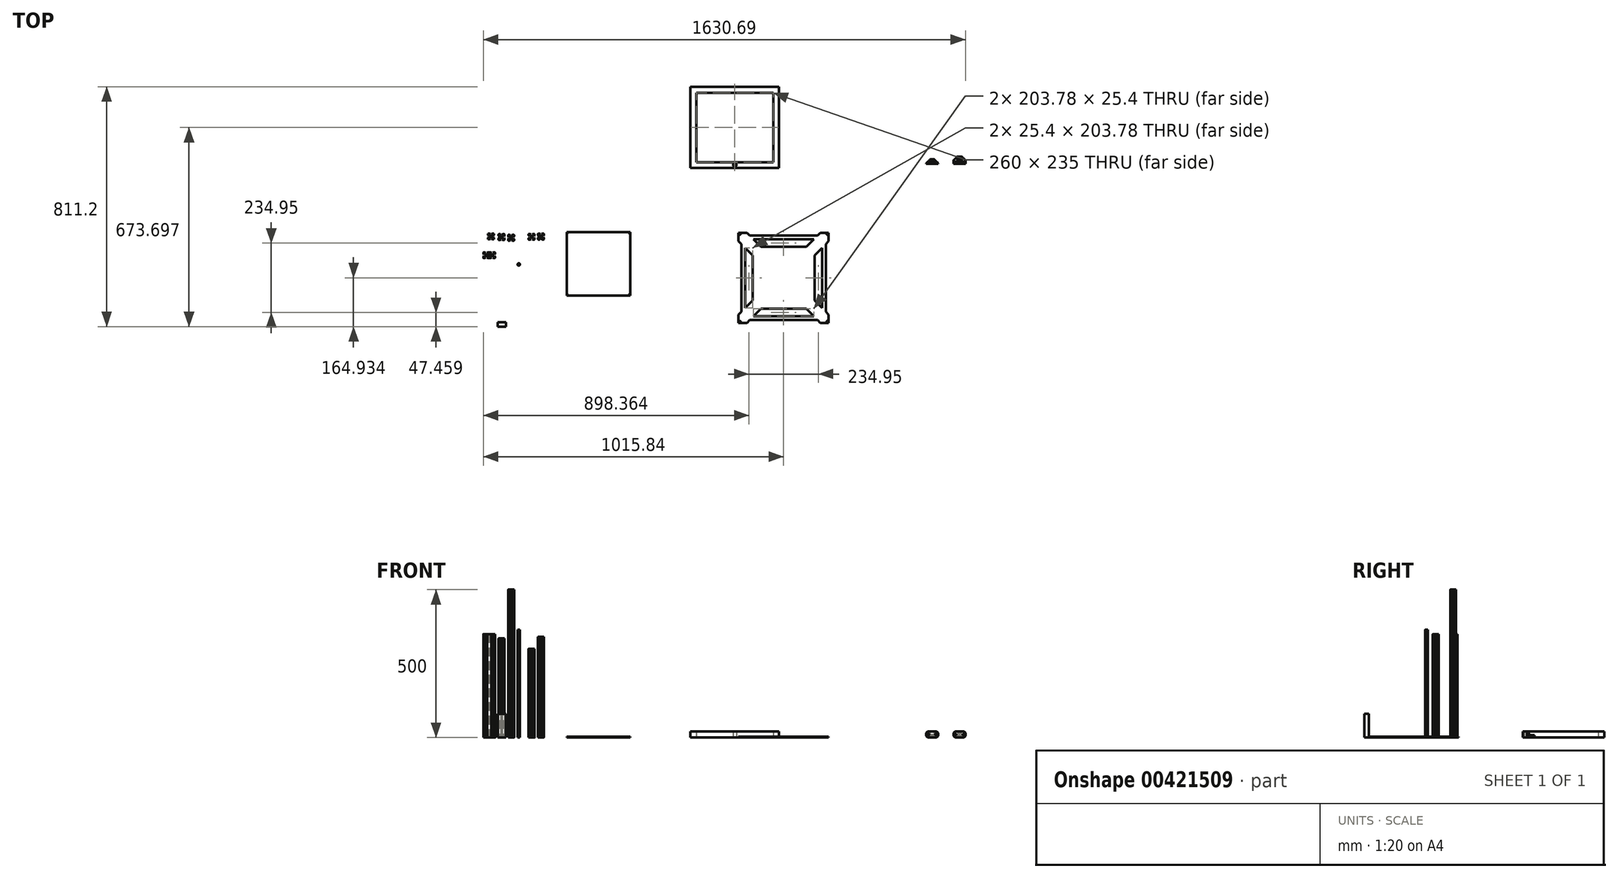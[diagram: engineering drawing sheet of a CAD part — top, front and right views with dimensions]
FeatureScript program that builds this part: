
annotation { "Feature Type Name" : "Feature", "Feature Type Description" : "" }
export const myFeature = defineFeature(function(context is Context, id is Id, definition is map)
    precondition{}
    {
        {
            var Q0;
            Q0=qCreatedBy(makeId("Top.planeOp"),FACE);
            var sketch = newSketch(context, id + "F0", { "sketchPlane" : qUnion([Q0])});
            skArc(sketch, "E0.0", {"start": v(-58.83, 50.5) * mm, "mid": v(-59.9, 50.06) * mm, "end": v(-60.33, 49) * mm});
            skLineSegment(sketch, "E1.0", {"start": v(-60.33, 49) * mm, "end": v(-60.33, 45.4) * mm});
            skLineSegment(sketch, "E2.0", {"start": v(-56.9, 48.7) * mm, "end": v(-58.53, 48.7) * mm});
            skLineSegment(sketch, "E3.0", {"start": v(-56.9, 48.16) * mm, "end": v(-56.9, 48.7) * mm});
            skLineSegment(sketch, "E4.0", {"start": v(-58, 47.07) * mm, "end": v(-56.9, 48.16) * mm});
            skLineSegment(sketch, "E5.0", {"start": v(-58.53, 47.07) * mm, "end": v(-58, 47.07) * mm});
            skLineSegment(sketch, "E6.0", {"start": v(-58.53, 48.7) * mm, "end": v(-58.53, 47.07) * mm});
            skArc(sketch, "E7.0", {"start": v(-54.68, 50.26) * mm, "mid": v(-54.93, 50.44) * mm, "end": v(-55.24, 50.5) * mm});
            skLineSegment(sketch, "E8.0", {"start": v(-55.24, 50.5) * mm, "end": v(-58.83, 50.5) * mm});
            skLineSegment(sketch, "E9.0", {"start": v(-55.83, 47.06) * mm, "end": v(-55.83, 48.7) * mm});
            skLineSegment(sketch, "E10.0", {"start": v(-55.83, 48.7) * mm, "end": v(-53.22, 48.7) * mm});
            skLineSegment(sketch, "E11.0", {"start": v(-53.22, 48.8) * mm, "end": v(-54.68, 50.26) * mm});
            skLineSegment(sketch, "E12.0", {"start": v(-53.22, 48.7) * mm, "end": v(-53.22, 48.8) * mm});
            skLineSegment(sketch, "E13.0", {"start": v(-52.67, 43.9) * mm, "end": v(-55.83, 47.06) * mm});
            skLineSegment(sketch, "E14.0", {"start": v(-56.9, 46) * mm, "end": v(-53.73, 42.84) * mm});
            skLineSegment(sketch, "E15.0", {"start": v(-58.53, 46) * mm, "end": v(-56.9, 46) * mm});
            skArc(sketch, "E16.0", {"start": v(-60.33, 45.4) * mm, "mid": v(-60.27, 45.1) * mm, "end": v(-60.1, 44.84) * mm});
            skLineSegment(sketch, "E17.0", {"start": v(-60.1, 44.84) * mm, "end": v(-58.64, 43.39) * mm});
            skLineSegment(sketch, "E18.0", {"start": v(-58.64, 43.39) * mm, "end": v(-58.53, 43.39) * mm});
            skLineSegment(sketch, "E19.0", {"start": v(-58.53, 43.39) * mm, "end": v(-58.53, 46) * mm});
            skLineSegment(sketch, "E20.0", {"start": v(-53.73, 42.84) * mm, "end": v(-53.73, 38.16) * mm});
            skLineSegment(sketch, "E21.0", {"start": v(-48, 43.9) * mm, "end": v(-52.67, 43.9) * mm});
            skCircle(sketch, "E22.0", {"center": v(-50.33, 40.5) * mm, "radius": 2.1 * mm});
            skLineSegment(sketch, "E23.0", {"start": v(-45.98, 50.26) * mm, "end": v(-47.44, 48.8) * mm});
            skLineSegment(sketch, "E24.0", {"start": v(-47.44, 48.7) * mm, "end": v(-44.83, 48.7) * mm});
            skLineSegment(sketch, "E25.0", {"start": v(-44.83, 48.7) * mm, "end": v(-44.83, 47.06) * mm});
            skLineSegment(sketch, "E26.0", {"start": v(-44.83, 47.06) * mm, "end": v(-48, 43.9) * mm});
            skLineSegment(sketch, "E27.0", {"start": v(-46.93, 42.84) * mm, "end": v(-43.77, 46) * mm});
            skLineSegment(sketch, "E28.0", {"start": v(-43.77, 46) * mm, "end": v(-42.13, 46) * mm});
            skLineSegment(sketch, "E29.0", {"start": v(-42.13, 46) * mm, "end": v(-42.13, 43.39) * mm});
            skLineSegment(sketch, "E30.0", {"start": v(-42.13, 47.07) * mm, "end": v(-42.13, 48.7) * mm});
            skLineSegment(sketch, "E31.0", {"start": v(-42.67, 47.07) * mm, "end": v(-42.13, 47.07) * mm});
            skLineSegment(sketch, "E32.0", {"start": v(-43.76, 48.16) * mm, "end": v(-42.67, 47.07) * mm});
            skLineSegment(sketch, "E33.0", {"start": v(-43.76, 48.7) * mm, "end": v(-43.76, 48.16) * mm});
            skLineSegment(sketch, "E34.0", {"start": v(-42.13, 48.7) * mm, "end": v(-43.76, 48.7) * mm});
            skArc(sketch, "E35.0", {"start": v(-45.42, 50.5) * mm, "mid": v(-45.73, 50.44) * mm, "end": v(-45.98, 50.26) * mm});
            skLineSegment(sketch, "E36.0", {"start": v(-41.83, 50.5) * mm, "end": v(-45.42, 50.5) * mm});
            skArc(sketch, "E37.0", {"start": v(-40.33, 49) * mm, "mid": v(-40.77, 50.06) * mm, "end": v(-41.83, 50.5) * mm});
            skLineSegment(sketch, "E38.0", {"start": v(-40.33, 45.4) * mm, "end": v(-40.33, 49) * mm});
            skArc(sketch, "E39.0", {"start": v(-40.56, 44.84) * mm, "mid": v(-40.4, 45.1) * mm, "end": v(-40.33, 45.4) * mm});
            skLineSegment(sketch, "E40.0", {"start": v(-42.02, 43.39) * mm, "end": v(-40.56, 44.84) * mm});
            skLineSegment(sketch, "E41.0", {"start": v(-42.13, 43.39) * mm, "end": v(-42.02, 43.39) * mm});
            skLineSegment(sketch, "E42.0", {"start": v(-46.93, 38.16) * mm, "end": v(-46.93, 42.84) * mm});
            skLineSegment(sketch, "E43.0", {"start": v(-43.77, 35) * mm, "end": v(-46.93, 38.16) * mm});
            skLineSegment(sketch, "E44.0", {"start": v(-42.13, 35) * mm, "end": v(-43.77, 35) * mm});
            skLineSegment(sketch, "E45.0", {"start": v(-42.13, 37.6) * mm, "end": v(-42.13, 35) * mm});
            skLineSegment(sketch, "E46.0", {"start": v(-42.02, 37.6) * mm, "end": v(-42.13, 37.6) * mm});
            skLineSegment(sketch, "E47.0", {"start": v(-40.56, 36.15) * mm, "end": v(-42.02, 37.6) * mm});
            skArc(sketch, "E48.0", {"start": v(-40.33, 35.59) * mm, "mid": v(-40.4, 35.9) * mm, "end": v(-40.56, 36.15) * mm});
            skLineSegment(sketch, "E49.0", {"start": v(-40.33, 32) * mm, "end": v(-40.33, 35.59) * mm});
            skLineSegment(sketch, "E50.0", {"start": v(-42.13, 33.93) * mm, "end": v(-42.67, 33.93) * mm});
            skLineSegment(sketch, "E51.0", {"start": v(-42.67, 33.93) * mm, "end": v(-43.76, 32.84) * mm});
            skLineSegment(sketch, "E52.0", {"start": v(-43.76, 32.84) * mm, "end": v(-43.76, 32.3) * mm});
            skLineSegment(sketch, "E53.0", {"start": v(-43.76, 32.3) * mm, "end": v(-42.13, 32.3) * mm});
            skLineSegment(sketch, "E54.0", {"start": v(-42.13, 32.3) * mm, "end": v(-42.13, 33.93) * mm});
            skArc(sketch, "E55.0", {"start": v(-41.83, 30.5) * mm, "mid": v(-40.77, 30.94) * mm, "end": v(-40.33, 32) * mm});
            skLineSegment(sketch, "E56.0.2", {"start": v(-53.73, 38.16) * mm, "end": v(-56.9, 35) * mm});
            skLineSegment(sketch, "E56.0.3", {"start": v(-56.9, 35) * mm, "end": v(-58.53, 35) * mm});
            skLineSegment(sketch, "E56.0.4", {"start": v(-58.53, 35) * mm, "end": v(-58.53, 37.6) * mm});
            skLineSegment(sketch, "E56.0.5", {"start": v(-58.53, 37.6) * mm, "end": v(-58.64, 37.6) * mm});
            skLineSegment(sketch, "E56.0.6", {"start": v(-58.64, 37.6) * mm, "end": v(-60.1, 36.15) * mm});
            skArc(sketch, "E56.0.7", {"start": v(-60.1, 36.15) * mm, "mid": v(-60.27, 35.9) * mm, "end": v(-60.33, 35.59) * mm});
            skLineSegment(sketch, "E56.0.8", {"start": v(-60.33, 35.59) * mm, "end": v(-60.33, 32) * mm});
            skArc(sketch, "E56.0.9", {"start": v(-60.33, 32) * mm, "mid": v(-59.9, 30.94) * mm, "end": v(-58.83, 30.5) * mm});
            skLineSegment(sketch, "E56.0.10", {"start": v(-58.83, 30.5) * mm, "end": v(-55.24, 30.5) * mm});
            skArc(sketch, "E56.0.11", {"start": v(-55.24, 30.5) * mm, "mid": v(-54.93, 30.56) * mm, "end": v(-54.68, 30.73) * mm});
            skLineSegment(sketch, "E56.0.12", {"start": v(-54.68, 30.73) * mm, "end": v(-53.22, 32.19) * mm});
            skLineSegment(sketch, "E56.0.13", {"start": v(-53.22, 32.19) * mm, "end": v(-53.22, 32.3) * mm});
            skLineSegment(sketch, "E56.0.14", {"start": v(-53.22, 32.3) * mm, "end": v(-55.83, 32.3) * mm});
            skLineSegment(sketch, "E56.0.15", {"start": v(-55.83, 32.3) * mm, "end": v(-55.83, 33.94) * mm});
            skLineSegment(sketch, "E56.0.16", {"start": v(-55.83, 33.94) * mm, "end": v(-52.67, 37.1) * mm});
            skLineSegment(sketch, "E56.0.17", {"start": v(-52.67, 37.1) * mm, "end": v(-48, 37.1) * mm});
            skLineSegment(sketch, "E56.0.18", {"start": v(-48, 37.1) * mm, "end": v(-44.83, 33.94) * mm});
            skLineSegment(sketch, "E56.0.19", {"start": v(-44.83, 33.94) * mm, "end": v(-44.83, 32.3) * mm});
            skLineSegment(sketch, "E56.0.20", {"start": v(-44.83, 32.3) * mm, "end": v(-47.44, 32.3) * mm});
            skLineSegment(sketch, "E56.0.21", {"start": v(-47.44, 32.3) * mm, "end": v(-47.44, 32.19) * mm});
            skLineSegment(sketch, "E56.0.22", {"start": v(-47.44, 32.19) * mm, "end": v(-45.98, 30.73) * mm});
            skArc(sketch, "E56.0.23", {"start": v(-45.98, 30.73) * mm, "mid": v(-45.73, 30.56) * mm, "end": v(-45.42, 30.5) * mm});
            skLineSegment(sketch, "E56.0.24", {"start": v(-45.42, 30.5) * mm, "end": v(-41.83, 30.5) * mm});
            skLineSegment(sketch, "E56.0.45", {"start": v(-47.44, 48.8) * mm, "end": v(-47.44, 48.7) * mm});
            skLineSegment(sketch, "E57.0", {"start": v(-58, 33.93) * mm, "end": v(-58.53, 33.93) * mm});
            skLineSegment(sketch, "E58.0", {"start": v(-58.53, 33.93) * mm, "end": v(-58.53, 32.3) * mm});
            skLineSegment(sketch, "E59.0", {"start": v(-58.53, 32.3) * mm, "end": v(-56.9, 32.3) * mm});
            skLineSegment(sketch, "E60.0", {"start": v(-56.9, 32.3) * mm, "end": v(-56.9, 32.84) * mm});
            skLineSegment(sketch, "E61.0", {"start": v(-56.9, 32.84) * mm, "end": v(-58, 33.93) * mm});
            skLineSegment(sketch, "E62", {"start": v(-60.33, 49) * mm, "end": v(-60.33, 50.5) * mm});
            skLineSegment(sketch, "E63", {"start": v(-60.33, 50.5) * mm, "end": v(-58.83, 50.5) * mm});
            skLineSegment(sketch, "E64", {"start": v(-41.83, 50.5) * mm, "end": v(-40.33, 50.5) * mm});
            skLineSegment(sketch, "E65", {"start": v(-40.33, 50.5) * mm, "end": v(-40.33, 49) * mm});
            skLineSegment(sketch, "E66", {"start": v(-40.33, 32) * mm, "end": v(-40.33, 30.5) * mm});
            skLineSegment(sketch, "E67", {"start": v(-40.33, 30.5) * mm, "end": v(-41.83, 30.5) * mm});
            skLineSegment(sketch, "E68", {"start": v(-58.83, 30.5) * mm, "end": v(-60.33, 30.5) * mm});
            skLineSegment(sketch, "E69", {"start": v(-60.33, 30.5) * mm, "end": v(-60.33, 32) * mm});
            skSolve(sketch);
        }
        {
            var Q0;
            Q0=qCreatedBy(makeId("Top.planeOp"),FACE);
            var sketch = newSketch(context, id + "F1", { "sketchPlane" : qUnion([Q0])});
            skArc(sketch, "E70.0", {"start": v(-23.11, 48.38) * mm, "mid": v(-24.17, 47.94) * mm, "end": v(-24.61, 46.88) * mm});
            skLineSegment(sketch, "E71.0", {"start": v(-24.61, 46.88) * mm, "end": v(-24.61, 43.29) * mm});
            skLineSegment(sketch, "E72.0", {"start": v(-21.18, 46.58) * mm, "end": v(-22.81, 46.58) * mm});
            skLineSegment(sketch, "E73.0", {"start": v(-21.18, 46.04) * mm, "end": v(-21.18, 46.58) * mm});
            skLineSegment(sketch, "E74.0", {"start": v(-22.27, 44.95) * mm, "end": v(-21.18, 46.04) * mm});
            skLineSegment(sketch, "E75.0", {"start": v(-22.81, 44.95) * mm, "end": v(-22.27, 44.95) * mm});
            skLineSegment(sketch, "E76.0", {"start": v(-22.81, 46.58) * mm, "end": v(-22.81, 44.95) * mm});
            skArc(sketch, "E77.0", {"start": v(-18.96, 48.15) * mm, "mid": v(-19.22, 48.32) * mm, "end": v(-19.52, 48.38) * mm});
            skLineSegment(sketch, "E78.0", {"start": v(-19.52, 48.38) * mm, "end": v(-23.11, 48.38) * mm});
            skLineSegment(sketch, "E79.0", {"start": v(-20.11, 44.94) * mm, "end": v(-20.11, 46.58) * mm});
            skLineSegment(sketch, "E80.0", {"start": v(-20.11, 46.58) * mm, "end": v(-17.5, 46.58) * mm});
            skLineSegment(sketch, "E81.0", {"start": v(-17.5, 46.7) * mm, "end": v(-18.96, 48.15) * mm});
            skLineSegment(sketch, "E82.0", {"start": v(-17.5, 46.58) * mm, "end": v(-17.5, 46.7) * mm});
            skLineSegment(sketch, "E83.0", {"start": v(-16.95, 41.78) * mm, "end": v(-20.11, 44.94) * mm});
            skLineSegment(sketch, "E84.0", {"start": v(-21.17, 43.88) * mm, "end": v(-18.01, 40.72) * mm});
            skLineSegment(sketch, "E85.0", {"start": v(-22.81, 43.88) * mm, "end": v(-21.17, 43.88) * mm});
            skArc(sketch, "E86.0", {"start": v(-24.61, 43.29) * mm, "mid": v(-24.55, 42.99) * mm, "end": v(-24.38, 42.73) * mm});
            skLineSegment(sketch, "E87.0", {"start": v(-24.38, 42.73) * mm, "end": v(-22.92, 41.27) * mm});
            skLineSegment(sketch, "E88.0", {"start": v(-22.92, 41.27) * mm, "end": v(-22.81, 41.27) * mm});
            skLineSegment(sketch, "E89.0", {"start": v(-22.81, 41.27) * mm, "end": v(-22.81, 43.88) * mm});
            skLineSegment(sketch, "E90.0", {"start": v(-18.01, 40.72) * mm, "end": v(-18.01, 36.04) * mm});
            skLineSegment(sketch, "E91.0", {"start": v(-12.27, 41.78) * mm, "end": v(-16.95, 41.78) * mm});
            skCircle(sketch, "E92.0", {"center": v(-14.61, 38.38) * mm, "radius": 2.1 * mm});
            skLineSegment(sketch, "E93.0", {"start": v(-10.26, 48.15) * mm, "end": v(-11.72, 46.7) * mm});
            skLineSegment(sketch, "E94.0", {"start": v(-11.72, 46.58) * mm, "end": v(-9.11, 46.58) * mm});
            skLineSegment(sketch, "E95.0", {"start": v(-9.11, 46.58) * mm, "end": v(-9.11, 44.94) * mm});
            skLineSegment(sketch, "E96.0", {"start": v(-9.11, 44.94) * mm, "end": v(-12.27, 41.78) * mm});
            skLineSegment(sketch, "E97.0", {"start": v(-11.21, 40.72) * mm, "end": v(-8.05, 43.88) * mm});
            skLineSegment(sketch, "E98.0", {"start": v(-8.05, 43.88) * mm, "end": v(-6.41, 43.88) * mm});
            skLineSegment(sketch, "E99.0", {"start": v(-6.41, 43.88) * mm, "end": v(-6.41, 41.27) * mm});
            skLineSegment(sketch, "E100.0", {"start": v(-6.41, 44.95) * mm, "end": v(-6.41, 46.58) * mm});
            skLineSegment(sketch, "E101.0", {"start": v(-6.95, 44.95) * mm, "end": v(-6.41, 44.95) * mm});
            skLineSegment(sketch, "E102.0", {"start": v(-8.04, 46.04) * mm, "end": v(-6.95, 44.95) * mm});
            skLineSegment(sketch, "E103.0", {"start": v(-8.04, 46.58) * mm, "end": v(-8.04, 46.04) * mm});
            skLineSegment(sketch, "E104.0", {"start": v(-6.41, 46.58) * mm, "end": v(-8.04, 46.58) * mm});
            skArc(sketch, "E105.0", {"start": v(-9.7, 48.38) * mm, "mid": v(-10, 48.32) * mm, "end": v(-10.26, 48.15) * mm});
            skLineSegment(sketch, "E106.0", {"start": v(-6.11, 48.38) * mm, "end": v(-9.7, 48.38) * mm});
            skArc(sketch, "E107.0", {"start": v(-4.61, 46.88) * mm, "mid": v(-5.05, 47.94) * mm, "end": v(-6.11, 48.38) * mm});
            skLineSegment(sketch, "E108.0", {"start": v(-4.61, 43.29) * mm, "end": v(-4.61, 46.88) * mm});
            skArc(sketch, "E109.0", {"start": v(-4.84, 42.73) * mm, "mid": v(-4.67, 42.99) * mm, "end": v(-4.61, 43.29) * mm});
            skLineSegment(sketch, "E110.0", {"start": v(-6.3, 41.27) * mm, "end": v(-4.84, 42.73) * mm});
            skLineSegment(sketch, "E111.0", {"start": v(-6.41, 41.27) * mm, "end": v(-6.3, 41.27) * mm});
            skLineSegment(sketch, "E112.0", {"start": v(-11.21, 36.04) * mm, "end": v(-11.21, 40.72) * mm});
            skLineSegment(sketch, "E113.0", {"start": v(-8.05, 32.88) * mm, "end": v(-11.21, 36.04) * mm});
            skLineSegment(sketch, "E114.0", {"start": v(-6.41, 32.88) * mm, "end": v(-8.05, 32.88) * mm});
            skLineSegment(sketch, "E115.0", {"start": v(-6.41, 35.5) * mm, "end": v(-6.41, 32.88) * mm});
            skLineSegment(sketch, "E116.0", {"start": v(-6.3, 35.5) * mm, "end": v(-6.41, 35.5) * mm});
            skLineSegment(sketch, "E117.0", {"start": v(-4.84, 34.03) * mm, "end": v(-6.3, 35.5) * mm});
            skArc(sketch, "E118.0", {"start": v(-4.61, 33.47) * mm, "mid": v(-4.67, 33.78) * mm, "end": v(-4.84, 34.03) * mm});
            skLineSegment(sketch, "E119.0", {"start": v(-4.61, 29.88) * mm, "end": v(-4.61, 33.47) * mm});
            skLineSegment(sketch, "E120.0", {"start": v(-6.41, 31.81) * mm, "end": v(-6.95, 31.81) * mm});
            skLineSegment(sketch, "E121.0", {"start": v(-6.95, 31.81) * mm, "end": v(-8.04, 30.72) * mm});
            skLineSegment(sketch, "E122.0", {"start": v(-8.04, 30.72) * mm, "end": v(-8.04, 30.18) * mm});
            skLineSegment(sketch, "E123.0", {"start": v(-8.04, 30.18) * mm, "end": v(-6.41, 30.18) * mm});
            skLineSegment(sketch, "E124.0", {"start": v(-6.41, 30.18) * mm, "end": v(-6.41, 31.81) * mm});
            skArc(sketch, "E125.0", {"start": v(-6.11, 28.38) * mm, "mid": v(-5.05, 28.82) * mm, "end": v(-4.61, 29.88) * mm});
            skLineSegment(sketch, "E126.0.2", {"start": v(-18.01, 36.04) * mm, "end": v(-21.17, 32.88) * mm});
            skLineSegment(sketch, "E126.0.3", {"start": v(-21.17, 32.88) * mm, "end": v(-22.81, 32.88) * mm});
            skLineSegment(sketch, "E126.0.4", {"start": v(-22.81, 32.88) * mm, "end": v(-22.81, 35.5) * mm});
            skLineSegment(sketch, "E126.0.5", {"start": v(-22.81, 35.5) * mm, "end": v(-22.92, 35.5) * mm});
            skLineSegment(sketch, "E126.0.6", {"start": v(-22.92, 35.5) * mm, "end": v(-24.38, 34.03) * mm});
            skArc(sketch, "E126.0.7", {"start": v(-24.38, 34.03) * mm, "mid": v(-24.55, 33.78) * mm, "end": v(-24.61, 33.47) * mm});
            skLineSegment(sketch, "E126.0.8", {"start": v(-24.61, 33.47) * mm, "end": v(-24.61, 29.88) * mm});
            skArc(sketch, "E126.0.9", {"start": v(-24.61, 29.88) * mm, "mid": v(-24.17, 28.82) * mm, "end": v(-23.11, 28.38) * mm});
            skLineSegment(sketch, "E126.0.10", {"start": v(-23.11, 28.38) * mm, "end": v(-19.52, 28.38) * mm});
            skArc(sketch, "E126.0.11", {"start": v(-19.52, 28.38) * mm, "mid": v(-19.22, 28.44) * mm, "end": v(-18.96, 28.61) * mm});
            skLineSegment(sketch, "E126.0.12", {"start": v(-18.96, 28.61) * mm, "end": v(-17.5, 30.07) * mm});
            skLineSegment(sketch, "E126.0.13", {"start": v(-17.5, 30.07) * mm, "end": v(-17.5, 30.18) * mm});
            skLineSegment(sketch, "E126.0.14", {"start": v(-17.5, 30.18) * mm, "end": v(-20.11, 30.18) * mm});
            skLineSegment(sketch, "E126.0.15", {"start": v(-20.11, 30.18) * mm, "end": v(-20.11, 31.82) * mm});
            skLineSegment(sketch, "E126.0.16", {"start": v(-20.11, 31.82) * mm, "end": v(-16.95, 34.98) * mm});
            skLineSegment(sketch, "E126.0.17", {"start": v(-16.95, 34.98) * mm, "end": v(-12.27, 34.98) * mm});
            skLineSegment(sketch, "E126.0.18", {"start": v(-12.27, 34.98) * mm, "end": v(-9.11, 31.82) * mm});
            skLineSegment(sketch, "E126.0.19", {"start": v(-9.11, 31.82) * mm, "end": v(-9.11, 30.18) * mm});
            skLineSegment(sketch, "E126.0.20", {"start": v(-9.11, 30.18) * mm, "end": v(-11.72, 30.18) * mm});
            skLineSegment(sketch, "E126.0.21", {"start": v(-11.72, 30.18) * mm, "end": v(-11.72, 30.07) * mm});
            skLineSegment(sketch, "E126.0.22", {"start": v(-11.72, 30.07) * mm, "end": v(-10.26, 28.61) * mm});
            skArc(sketch, "E126.0.23", {"start": v(-10.26, 28.61) * mm, "mid": v(-10, 28.44) * mm, "end": v(-9.7, 28.38) * mm});
            skLineSegment(sketch, "E126.0.24", {"start": v(-9.7, 28.38) * mm, "end": v(-6.11, 28.38) * mm});
            skLineSegment(sketch, "E126.0.45", {"start": v(-11.72, 46.7) * mm, "end": v(-11.72, 46.58) * mm});
            skLineSegment(sketch, "E127.0", {"start": v(-22.27, 31.81) * mm, "end": v(-22.81, 31.81) * mm});
            skLineSegment(sketch, "E128.0", {"start": v(-22.81, 31.81) * mm, "end": v(-22.81, 30.18) * mm});
            skLineSegment(sketch, "E129.0", {"start": v(-22.81, 30.18) * mm, "end": v(-21.18, 30.18) * mm});
            skLineSegment(sketch, "E130.0", {"start": v(-21.18, 30.18) * mm, "end": v(-21.18, 30.72) * mm});
            skLineSegment(sketch, "E131.0", {"start": v(-21.18, 30.72) * mm, "end": v(-22.27, 31.81) * mm});
            skSolve(sketch);
        }
        {
            var Q0;
            Q0=qCreatedBy(makeId("Top.planeOp"),FACE);
            var sketch = newSketch(context, id + "F2", { "sketchPlane" : qUnion([Q0])});
            skArc(sketch, "E132.0", {"start": v(9.31, 46.03) * mm, "mid": v(8.25, 45.6) * mm, "end": v(7.81, 44.53) * mm});
            skLineSegment(sketch, "E133.0", {"start": v(7.81, 44.53) * mm, "end": v(7.81, 40.94) * mm});
            skLineSegment(sketch, "E134.0", {"start": v(11.24, 44.23) * mm, "end": v(9.61, 44.23) * mm});
            skLineSegment(sketch, "E135.0", {"start": v(11.24, 43.7) * mm, "end": v(11.24, 44.23) * mm});
            skLineSegment(sketch, "E136.0", {"start": v(10.15, 42.6) * mm, "end": v(11.24, 43.7) * mm});
            skLineSegment(sketch, "E137.0", {"start": v(9.61, 42.6) * mm, "end": v(10.15, 42.6) * mm});
            skLineSegment(sketch, "E138.0", {"start": v(9.61, 44.23) * mm, "end": v(9.61, 42.6) * mm});
            skArc(sketch, "E139.0", {"start": v(13.46, 45.8) * mm, "mid": v(13.2, 45.97) * mm, "end": v(12.9, 46.03) * mm});
            skLineSegment(sketch, "E140.0", {"start": v(12.9, 46.03) * mm, "end": v(9.31, 46.03) * mm});
            skLineSegment(sketch, "E141.0", {"start": v(12.31, 42.6) * mm, "end": v(12.31, 44.23) * mm});
            skLineSegment(sketch, "E142.0", {"start": v(12.31, 44.23) * mm, "end": v(14.92, 44.23) * mm});
            skLineSegment(sketch, "E143.0", {"start": v(14.92, 44.34) * mm, "end": v(13.46, 45.8) * mm});
            skLineSegment(sketch, "E144.0", {"start": v(14.92, 44.23) * mm, "end": v(14.92, 44.34) * mm});
            skLineSegment(sketch, "E145.0", {"start": v(15.47, 39.43) * mm, "end": v(12.31, 42.6) * mm});
            skLineSegment(sketch, "E146.0", {"start": v(11.25, 41.53) * mm, "end": v(14.41, 38.37) * mm});
            skLineSegment(sketch, "E147.0", {"start": v(9.61, 41.53) * mm, "end": v(11.25, 41.53) * mm});
            skArc(sketch, "E148.0", {"start": v(7.81, 40.94) * mm, "mid": v(7.87, 40.64) * mm, "end": v(8.04, 40.38) * mm});
            skLineSegment(sketch, "E149.0", {"start": v(8.04, 40.38) * mm, "end": v(9.5, 38.92) * mm});
            skLineSegment(sketch, "E150.0", {"start": v(9.5, 38.92) * mm, "end": v(9.61, 38.92) * mm});
            skLineSegment(sketch, "E151.0", {"start": v(9.61, 38.92) * mm, "end": v(9.61, 41.53) * mm});
            skLineSegment(sketch, "E152.0", {"start": v(14.41, 38.37) * mm, "end": v(14.41, 33.7) * mm});
            skLineSegment(sketch, "E153.0", {"start": v(20.15, 39.43) * mm, "end": v(15.47, 39.43) * mm});
            skCircle(sketch, "E154.0", {"center": v(17.81, 36.03) * mm, "radius": 2.1 * mm});
            skLineSegment(sketch, "E155.0", {"start": v(22.16, 45.8) * mm, "end": v(20.7, 44.34) * mm});
            skLineSegment(sketch, "E156.0", {"start": v(20.7, 44.23) * mm, "end": v(23.31, 44.23) * mm});
            skLineSegment(sketch, "E157.0", {"start": v(23.31, 44.23) * mm, "end": v(23.31, 42.6) * mm});
            skLineSegment(sketch, "E158.0", {"start": v(23.31, 42.6) * mm, "end": v(20.15, 39.43) * mm});
            skLineSegment(sketch, "E159.0", {"start": v(21.21, 38.37) * mm, "end": v(24.37, 41.53) * mm});
            skLineSegment(sketch, "E160.0", {"start": v(24.37, 41.53) * mm, "end": v(26.01, 41.53) * mm});
            skLineSegment(sketch, "E161.0", {"start": v(26.01, 41.53) * mm, "end": v(26.01, 38.92) * mm});
            skLineSegment(sketch, "E162.0", {"start": v(26.01, 42.6) * mm, "end": v(26.01, 44.23) * mm});
            skLineSegment(sketch, "E163.0", {"start": v(25.47, 42.6) * mm, "end": v(26.01, 42.6) * mm});
            skLineSegment(sketch, "E164.0", {"start": v(24.38, 43.7) * mm, "end": v(25.47, 42.6) * mm});
            skLineSegment(sketch, "E165.0", {"start": v(24.38, 44.23) * mm, "end": v(24.38, 43.7) * mm});
            skLineSegment(sketch, "E166.0", {"start": v(26.01, 44.23) * mm, "end": v(24.38, 44.23) * mm});
            skArc(sketch, "E167.0", {"start": v(22.72, 46.03) * mm, "mid": v(22.42, 45.97) * mm, "end": v(22.16, 45.8) * mm});
            skLineSegment(sketch, "E168.0", {"start": v(26.31, 46.03) * mm, "end": v(22.72, 46.03) * mm});
            skArc(sketch, "E169.0", {"start": v(27.81, 44.53) * mm, "mid": v(27.37, 45.6) * mm, "end": v(26.31, 46.03) * mm});
            skLineSegment(sketch, "E170.0", {"start": v(27.81, 40.94) * mm, "end": v(27.81, 44.53) * mm});
            skArc(sketch, "E171.0", {"start": v(27.58, 40.38) * mm, "mid": v(27.75, 40.64) * mm, "end": v(27.81, 40.94) * mm});
            skLineSegment(sketch, "E172.0", {"start": v(26.12, 38.92) * mm, "end": v(27.58, 40.38) * mm});
            skLineSegment(sketch, "E173.0", {"start": v(26.01, 38.92) * mm, "end": v(26.12, 38.92) * mm});
            skLineSegment(sketch, "E174.0", {"start": v(21.21, 33.7) * mm, "end": v(21.21, 38.37) * mm});
            skLineSegment(sketch, "E175.0", {"start": v(24.37, 30.53) * mm, "end": v(21.21, 33.7) * mm});
            skLineSegment(sketch, "E176.0", {"start": v(26.01, 30.53) * mm, "end": v(24.37, 30.53) * mm});
            skLineSegment(sketch, "E177.0", {"start": v(26.01, 33.14) * mm, "end": v(26.01, 30.53) * mm});
            skLineSegment(sketch, "E178.0", {"start": v(26.12, 33.14) * mm, "end": v(26.01, 33.14) * mm});
            skLineSegment(sketch, "E179.0", {"start": v(27.58, 31.68) * mm, "end": v(26.12, 33.14) * mm});
            skArc(sketch, "E180.0", {"start": v(27.81, 31.12) * mm, "mid": v(27.75, 31.43) * mm, "end": v(27.58, 31.68) * mm});
            skLineSegment(sketch, "E181.0", {"start": v(27.81, 27.53) * mm, "end": v(27.81, 31.12) * mm});
            skLineSegment(sketch, "E182.0", {"start": v(26.01, 29.46) * mm, "end": v(25.47, 29.46) * mm});
            skLineSegment(sketch, "E183.0", {"start": v(25.47, 29.46) * mm, "end": v(24.38, 28.37) * mm});
            skLineSegment(sketch, "E184.0", {"start": v(24.38, 28.37) * mm, "end": v(24.38, 27.83) * mm});
            skLineSegment(sketch, "E185.0", {"start": v(24.38, 27.83) * mm, "end": v(26.01, 27.83) * mm});
            skLineSegment(sketch, "E186.0", {"start": v(26.01, 27.83) * mm, "end": v(26.01, 29.46) * mm});
            skArc(sketch, "E187.0", {"start": v(26.31, 26.03) * mm, "mid": v(27.37, 26.47) * mm, "end": v(27.81, 27.53) * mm});
            skLineSegment(sketch, "E188.0.2", {"start": v(14.41, 33.7) * mm, "end": v(11.25, 30.53) * mm});
            skLineSegment(sketch, "E188.0.3", {"start": v(11.25, 30.53) * mm, "end": v(9.61, 30.53) * mm});
            skLineSegment(sketch, "E188.0.4", {"start": v(9.61, 30.53) * mm, "end": v(9.61, 33.14) * mm});
            skLineSegment(sketch, "E188.0.5", {"start": v(9.61, 33.14) * mm, "end": v(9.5, 33.14) * mm});
            skLineSegment(sketch, "E188.0.6", {"start": v(9.5, 33.14) * mm, "end": v(8.04, 31.68) * mm});
            skArc(sketch, "E188.0.7", {"start": v(8.04, 31.68) * mm, "mid": v(7.87, 31.43) * mm, "end": v(7.81, 31.12) * mm});
            skLineSegment(sketch, "E188.0.8", {"start": v(7.81, 31.12) * mm, "end": v(7.81, 27.53) * mm});
            skArc(sketch, "E188.0.9", {"start": v(7.81, 27.53) * mm, "mid": v(8.25, 26.47) * mm, "end": v(9.31, 26.03) * mm});
            skLineSegment(sketch, "E188.0.10", {"start": v(9.31, 26.03) * mm, "end": v(12.9, 26.03) * mm});
            skArc(sketch, "E188.0.11", {"start": v(12.9, 26.03) * mm, "mid": v(13.2, 26.1) * mm, "end": v(13.46, 26.26) * mm});
            skLineSegment(sketch, "E188.0.12", {"start": v(13.46, 26.26) * mm, "end": v(14.92, 27.72) * mm});
            skLineSegment(sketch, "E188.0.13", {"start": v(14.92, 27.72) * mm, "end": v(14.92, 27.83) * mm});
            skLineSegment(sketch, "E188.0.14", {"start": v(14.92, 27.83) * mm, "end": v(12.31, 27.83) * mm});
            skLineSegment(sketch, "E188.0.15", {"start": v(12.31, 27.83) * mm, "end": v(12.31, 29.47) * mm});
            skLineSegment(sketch, "E188.0.16", {"start": v(12.31, 29.47) * mm, "end": v(15.47, 32.63) * mm});
            skLineSegment(sketch, "E188.0.17", {"start": v(15.47, 32.63) * mm, "end": v(20.15, 32.63) * mm});
            skLineSegment(sketch, "E188.0.18", {"start": v(20.15, 32.63) * mm, "end": v(23.31, 29.47) * mm});
            skLineSegment(sketch, "E188.0.19", {"start": v(23.31, 29.47) * mm, "end": v(23.31, 27.83) * mm});
            skLineSegment(sketch, "E188.0.20", {"start": v(23.31, 27.83) * mm, "end": v(20.7, 27.83) * mm});
            skLineSegment(sketch, "E188.0.21", {"start": v(20.7, 27.83) * mm, "end": v(20.7, 27.72) * mm});
            skLineSegment(sketch, "E188.0.22", {"start": v(20.7, 27.72) * mm, "end": v(22.16, 26.26) * mm});
            skArc(sketch, "E188.0.23", {"start": v(22.16, 26.26) * mm, "mid": v(22.42, 26.1) * mm, "end": v(22.72, 26.03) * mm});
            skLineSegment(sketch, "E188.0.24", {"start": v(22.72, 26.03) * mm, "end": v(26.31, 26.03) * mm});
            skLineSegment(sketch, "E188.0.45", {"start": v(20.7, 44.34) * mm, "end": v(20.7, 44.23) * mm});
            skLineSegment(sketch, "E189.0", {"start": v(10.15, 29.46) * mm, "end": v(9.61, 29.46) * mm});
            skLineSegment(sketch, "E190.0", {"start": v(9.61, 29.46) * mm, "end": v(9.61, 27.83) * mm});
            skLineSegment(sketch, "E191.0", {"start": v(9.61, 27.83) * mm, "end": v(11.24, 27.83) * mm});
            skLineSegment(sketch, "E192.0", {"start": v(11.24, 27.83) * mm, "end": v(11.24, 28.37) * mm});
            skLineSegment(sketch, "E193.0", {"start": v(11.24, 28.37) * mm, "end": v(10.15, 29.46) * mm});
            skSolve(sketch);
        }
        {
            var Q0;
            Q0=qCreatedBy(makeId("Top.planeOp"),FACE);
            var sketch = newSketch(context, id + "F3", { "sketchPlane" : qUnion([Q0])});
            skArc(sketch, "E194.0", {"start": v(-74.8, -12.95) * mm, "mid": v(-75.87, -13.39) * mm, "end": v(-76.3, -14.45) * mm});
            skLineSegment(sketch, "E195.0", {"start": v(-76.3, -14.45) * mm, "end": v(-76.3, -18.04) * mm});
            skLineSegment(sketch, "E196.0", {"start": v(-72.88, -14.75) * mm, "end": v(-74.5, -14.75) * mm});
            skLineSegment(sketch, "E197.0", {"start": v(-72.88, -15.29) * mm, "end": v(-72.88, -14.75) * mm});
            skLineSegment(sketch, "E198.0", {"start": v(-73.97, -16.38) * mm, "end": v(-72.88, -15.29) * mm});
            skLineSegment(sketch, "E199.0", {"start": v(-74.5, -16.38) * mm, "end": v(-73.97, -16.38) * mm});
            skLineSegment(sketch, "E200.0", {"start": v(-74.5, -14.75) * mm, "end": v(-74.5, -16.38) * mm});
            skArc(sketch, "E201.0", {"start": v(-70.66, -13.18) * mm, "mid": v(-70.91, -13) * mm, "end": v(-71.22, -12.95) * mm});
            skLineSegment(sketch, "E202.0", {"start": v(-71.22, -12.95) * mm, "end": v(-74.8, -12.95) * mm});
            skLineSegment(sketch, "E203.0", {"start": v(-71.8, -16.39) * mm, "end": v(-71.8, -14.75) * mm});
            skLineSegment(sketch, "E204.0", {"start": v(-71.8, -14.75) * mm, "end": v(-69.2, -14.75) * mm});
            skLineSegment(sketch, "E205.0", {"start": v(-69.2, -14.64) * mm, "end": v(-70.66, -13.18) * mm});
            skLineSegment(sketch, "E206.0", {"start": v(-69.2, -14.75) * mm, "end": v(-69.2, -14.64) * mm});
            skLineSegment(sketch, "E207.0", {"start": v(-68.65, -19.55) * mm, "end": v(-71.8, -16.39) * mm});
            skLineSegment(sketch, "E208.0", {"start": v(-72.87, -17.45) * mm, "end": v(-69.7, -20.6) * mm});
            skLineSegment(sketch, "E209.0", {"start": v(-74.5, -17.45) * mm, "end": v(-72.87, -17.45) * mm});
            skArc(sketch, "E210.0", {"start": v(-76.3, -18.04) * mm, "mid": v(-76.25, -18.34) * mm, "end": v(-76.08, -18.6) * mm});
            skLineSegment(sketch, "E211.0", {"start": v(-76.08, -18.6) * mm, "end": v(-74.62, -20.06) * mm});
            skLineSegment(sketch, "E212.0", {"start": v(-74.62, -20.06) * mm, "end": v(-74.5, -20.06) * mm});
            skLineSegment(sketch, "E213.0", {"start": v(-74.5, -20.06) * mm, "end": v(-74.5, -17.45) * mm});
            skLineSegment(sketch, "E214.0", {"start": v(-69.7, -20.6) * mm, "end": v(-69.7, -25.29) * mm});
            skLineSegment(sketch, "E215.0", {"start": v(-63.97, -19.55) * mm, "end": v(-68.65, -19.55) * mm});
            skCircle(sketch, "E216.0", {"center": v(-66.3, -22.95) * mm, "radius": 2.1 * mm});
            skLineSegment(sketch, "E217.0", {"start": v(-61.96, -13.18) * mm, "end": v(-63.42, -14.64) * mm});
            skLineSegment(sketch, "E218.0", {"start": v(-63.42, -14.75) * mm, "end": v(-60.8, -14.75) * mm});
            skLineSegment(sketch, "E219.0", {"start": v(-60.8, -14.75) * mm, "end": v(-60.8, -16.39) * mm});
            skLineSegment(sketch, "E220.0", {"start": v(-60.8, -16.39) * mm, "end": v(-63.97, -19.55) * mm});
            skLineSegment(sketch, "E221.0", {"start": v(-62.9, -20.6) * mm, "end": v(-59.75, -17.45) * mm});
            skLineSegment(sketch, "E222.0", {"start": v(-59.75, -17.45) * mm, "end": v(-58.1, -17.45) * mm});
            skLineSegment(sketch, "E223.0", {"start": v(-58.1, -16.38) * mm, "end": v(-58.1, -14.75) * mm});
            skLineSegment(sketch, "E224.0", {"start": v(-58.65, -16.38) * mm, "end": v(-58.1, -16.38) * mm});
            skLineSegment(sketch, "E225.0", {"start": v(-59.74, -15.29) * mm, "end": v(-58.65, -16.38) * mm});
            skLineSegment(sketch, "E226.0", {"start": v(-59.74, -14.75) * mm, "end": v(-59.74, -15.29) * mm});
            skLineSegment(sketch, "E227.0", {"start": v(-58.1, -14.75) * mm, "end": v(-59.74, -14.75) * mm});
            skArc(sketch, "E228.0", {"start": v(-61.4, -12.95) * mm, "mid": v(-61.7, -13) * mm, "end": v(-61.96, -13.18) * mm});
            skLineSegment(sketch, "E229.0", {"start": v(-57.8, -12.95) * mm, "end": v(-61.4, -12.95) * mm});
            skLineSegment(sketch, "E230.0", {"start": v(-62.9, -25.29) * mm, "end": v(-62.9, -23.7) * mm});
            skLineSegment(sketch, "E231.0", {"start": v(-59.75, -28.45) * mm, "end": v(-62.9, -25.29) * mm});
            skLineSegment(sketch, "E232.0", {"start": v(-58.1, -28.45) * mm, "end": v(-59.75, -28.45) * mm});
            skLineSegment(sketch, "E233.0", {"start": v(-58.1, -29.52) * mm, "end": v(-58.65, -29.52) * mm});
            skLineSegment(sketch, "E234.0", {"start": v(-58.65, -29.52) * mm, "end": v(-59.74, -30.6) * mm});
            skLineSegment(sketch, "E235.0", {"start": v(-59.74, -30.6) * mm, "end": v(-59.74, -31.15) * mm});
            skLineSegment(sketch, "E236.0", {"start": v(-59.74, -31.15) * mm, "end": v(-58.1, -31.15) * mm});
            skLineSegment(sketch, "E237.0", {"start": v(-58.1, -31.15) * mm, "end": v(-58.1, -29.52) * mm});
            skLineSegment(sketch, "E238.0.2", {"start": v(-69.7, -25.29) * mm, "end": v(-72.87, -28.45) * mm});
            skLineSegment(sketch, "E238.0.3", {"start": v(-72.87, -28.45) * mm, "end": v(-74.5, -28.45) * mm});
            skLineSegment(sketch, "E238.0.4", {"start": v(-74.5, -28.45) * mm, "end": v(-74.5, -25.84) * mm});
            skLineSegment(sketch, "E238.0.5", {"start": v(-74.5, -25.84) * mm, "end": v(-74.62, -25.84) * mm});
            skLineSegment(sketch, "E238.0.6", {"start": v(-74.62, -25.84) * mm, "end": v(-76.08, -27.3) * mm});
            skArc(sketch, "E238.0.7", {"start": v(-76.08, -27.3) * mm, "mid": v(-76.25, -27.55) * mm, "end": v(-76.3, -27.86) * mm});
            skLineSegment(sketch, "E238.0.8", {"start": v(-76.3, -27.86) * mm, "end": v(-76.3, -31.45) * mm});
            skArc(sketch, "E238.0.9", {"start": v(-76.3, -31.45) * mm, "mid": v(-75.87, -32.5) * mm, "end": v(-74.8, -32.95) * mm});
            skLineSegment(sketch, "E238.0.10", {"start": v(-74.8, -32.95) * mm, "end": v(-71.22, -32.95) * mm});
            skArc(sketch, "E238.0.11", {"start": v(-71.22, -32.95) * mm, "mid": v(-70.91, -32.89) * mm, "end": v(-70.66, -32.72) * mm});
            skLineSegment(sketch, "E238.0.12", {"start": v(-70.66, -32.72) * mm, "end": v(-69.2, -31.26) * mm});
            skLineSegment(sketch, "E238.0.13", {"start": v(-69.2, -31.26) * mm, "end": v(-69.2, -31.15) * mm});
            skLineSegment(sketch, "E238.0.14", {"start": v(-69.2, -31.15) * mm, "end": v(-71.8, -31.15) * mm});
            skLineSegment(sketch, "E238.0.15", {"start": v(-71.8, -31.15) * mm, "end": v(-71.8, -29.5) * mm});
            skLineSegment(sketch, "E238.0.16", {"start": v(-71.8, -29.5) * mm, "end": v(-68.65, -26.35) * mm});
            skLineSegment(sketch, "E238.0.17", {"start": v(-68.65, -26.35) * mm, "end": v(-63.97, -26.35) * mm});
            skLineSegment(sketch, "E238.0.18", {"start": v(-63.97, -26.35) * mm, "end": v(-60.8, -29.5) * mm});
            skLineSegment(sketch, "E238.0.19", {"start": v(-60.8, -29.5) * mm, "end": v(-60.8, -31.15) * mm});
            skLineSegment(sketch, "E238.0.20", {"start": v(-60.8, -31.15) * mm, "end": v(-63.42, -31.15) * mm});
            skLineSegment(sketch, "E238.0.21", {"start": v(-63.42, -31.15) * mm, "end": v(-63.42, -31.26) * mm});
            skLineSegment(sketch, "E238.0.22", {"start": v(-63.42, -31.26) * mm, "end": v(-61.96, -32.72) * mm});
            skArc(sketch, "E238.0.23", {"start": v(-61.96, -32.72) * mm, "mid": v(-61.7, -32.89) * mm, "end": v(-61.4, -32.95) * mm});
            skLineSegment(sketch, "E238.0.24", {"start": v(-61.4, -32.95) * mm, "end": v(-57.8, -32.95) * mm});
            skLineSegment(sketch, "E238.0.45", {"start": v(-63.42, -14.64) * mm, "end": v(-63.42, -14.75) * mm});
            skLineSegment(sketch, "E239.0", {"start": v(-73.97, -29.52) * mm, "end": v(-74.5, -29.52) * mm});
            skLineSegment(sketch, "E240.0", {"start": v(-74.5, -29.52) * mm, "end": v(-74.5, -31.15) * mm});
            skLineSegment(sketch, "E241.0", {"start": v(-74.5, -31.15) * mm, "end": v(-72.88, -31.15) * mm});
            skLineSegment(sketch, "E242.0", {"start": v(-72.88, -31.15) * mm, "end": v(-72.88, -30.6) * mm});
            skLineSegment(sketch, "E243.0", {"start": v(-72.88, -30.6) * mm, "end": v(-73.97, -29.52) * mm});
            skArc(sketch, "E244.MirrorCS", {"start": v(-41.96, -13.18) * mm, "mid": v(-41.7, -13) * mm, "end": v(-41.4, -12.95) * mm});
            skArc(sketch, "E245.MirrorCS", {"start": v(-36.3, -18.04) * mm, "mid": v(-36.37, -18.34) * mm, "end": v(-36.54, -18.6) * mm});
            skLineSegment(sketch, "E246.MirrorCS", {"start": v(-38, -20.06) * mm, "end": v(-38.1, -20.06) * mm});
            skArc(sketch, "E247.MirrorCS", {"start": v(-51.22, -12.95) * mm, "mid": v(-50.91, -13) * mm, "end": v(-50.66, -13.18) * mm});
            skLineSegment(sketch, "E248.MirrorCS", {"start": v(-43.42, -14.75) * mm, "end": v(-43.42, -14.64) * mm});
            skLineSegment(sketch, "E249.MirrorCS", {"start": v(-43.42, -31.26) * mm, "end": v(-43.42, -31.15) * mm});
            skLineSegment(sketch, "E250.MirrorCS", {"start": v(-49.2, -31.15) * mm, "end": v(-49.2, -31.26) * mm});
            skLineSegment(sketch, "E251.MirrorCS", {"start": v(-49.2, -14.64) * mm, "end": v(-49.2, -14.75) * mm});
            skLineSegment(sketch, "E252.MirrorCS", {"start": v(-53.97, -16.38) * mm, "end": v(-54.5, -16.38) * mm});
            skArc(sketch, "E253.MirrorCS", {"start": v(-50.66, -32.72) * mm, "mid": v(-50.91, -32.89) * mm, "end": v(-51.22, -32.95) * mm});
            skArc(sketch, "E254.MirrorCS", {"start": v(-36.54, -27.3) * mm, "mid": v(-36.37, -27.55) * mm, "end": v(-36.3, -27.86) * mm});
            skLineSegment(sketch, "E255.MirrorCS", {"start": v(-52.88, -15.29) * mm, "end": v(-53.97, -16.38) * mm});
            skLineSegment(sketch, "E256.MirrorCS", {"start": v(-52.88, -14.75) * mm, "end": v(-52.88, -15.29) * mm});
            skLineSegment(sketch, "E257.MirrorCS", {"start": v(-38.65, -29.52) * mm, "end": v(-38.1, -29.52) * mm});
            skLineSegment(sketch, "E258.MirrorCS", {"start": v(-54.5, -29.52) * mm, "end": v(-53.97, -29.52) * mm});
            skArc(sketch, "E259.MirrorCS", {"start": v(-41.4, -32.95) * mm, "mid": v(-41.7, -32.89) * mm, "end": v(-41.96, -32.72) * mm});
            skLineSegment(sketch, "E260.MirrorCS", {"start": v(-39.74, -15.29) * mm, "end": v(-39.74, -14.75) * mm});
            skLineSegment(sketch, "E261.MirrorCS", {"start": v(-38.1, -16.38) * mm, "end": v(-38.65, -16.38) * mm});
            skLineSegment(sketch, "E262.MirrorCS", {"start": v(-39.74, -31.15) * mm, "end": v(-39.74, -30.6) * mm});
            skLineSegment(sketch, "E263.MirrorCS", {"start": v(-52.88, -30.6) * mm, "end": v(-52.88, -31.15) * mm});
            skLineSegment(sketch, "E264.MirrorCS", {"start": v(-38.1, -25.84) * mm, "end": v(-38, -25.84) * mm});
            skLineSegment(sketch, "E265.MirrorCS", {"start": v(-38.1, -20.06) * mm, "end": v(-38.1, -17.45) * mm});
            skLineSegment(sketch, "E266.MirrorCS", {"start": v(-49.2, -14.75) * mm, "end": v(-51.8, -14.75) * mm});
            skLineSegment(sketch, "E267.MirrorCS", {"start": v(-41.4, -12.95) * mm, "end": v(-37.8, -12.95) * mm});
            skLineSegment(sketch, "E268.MirrorCS", {"start": v(-50.66, -13.18) * mm, "end": v(-49.2, -14.64) * mm});
            skLineSegment(sketch, "E269.MirrorCS", {"start": v(-54.5, -28.45) * mm, "end": v(-52.87, -28.45) * mm});
            skLineSegment(sketch, "E270.MirrorCS", {"start": v(-38.1, -17.45) * mm, "end": v(-39.75, -17.45) * mm});
            skLineSegment(sketch, "E271.MirrorCS", {"start": v(-51.8, -14.75) * mm, "end": v(-51.8, -16.39) * mm});
            skArc(sketch, "E272.MirrorCS", {"start": v(-37.8, -12.95) * mm, "mid": v(-36.75, -13.39) * mm, "end": v(-36.3, -14.45) * mm});
            skLineSegment(sketch, "E273.MirrorCS", {"start": v(-52.87, -28.45) * mm, "end": v(-49.7, -25.29) * mm});
            skLineSegment(sketch, "E274.MirrorCS", {"start": v(-39.75, -17.45) * mm, "end": v(-42.9, -20.6) * mm});
            skLineSegment(sketch, "E275.MirrorCS", {"start": v(-36.54, -18.6) * mm, "end": v(-38, -20.06) * mm});
            skLineSegment(sketch, "E276.MirrorCS", {"start": v(-51.8, -16.39) * mm, "end": v(-48.65, -19.55) * mm});
            skLineSegment(sketch, "E277.MirrorCS", {"start": v(-49.7, -25.29) * mm, "end": v(-49.7, -23.7) * mm});
            skLineSegment(sketch, "E278.MirrorCS", {"start": v(-42.9, -20.6) * mm, "end": v(-42.9, -25.29) * mm});
            skLineSegment(sketch, "E279.MirrorCS", {"start": v(-48.65, -19.55) * mm, "end": v(-43.97, -19.55) * mm});
            skLineSegment(sketch, "E280.MirrorCS", {"start": v(-36.3, -14.45) * mm, "end": v(-36.3, -18.04) * mm});
            skLineSegment(sketch, "E281.MirrorCS", {"start": v(-54.8, -12.95) * mm, "end": v(-51.22, -12.95) * mm});
            skLineSegment(sketch, "E282.MirrorCS", {"start": v(-49.7, -20.6) * mm, "end": v(-52.87, -17.45) * mm});
            skLineSegment(sketch, "E283.MirrorCS", {"start": v(-43.97, -19.55) * mm, "end": v(-40.8, -16.39) * mm});
            skLineSegment(sketch, "E284.MirrorCS", {"start": v(-52.87, -17.45) * mm, "end": v(-54.5, -17.45) * mm});
            skLineSegment(sketch, "E285.MirrorCS", {"start": v(-40.8, -16.39) * mm, "end": v(-40.8, -14.75) * mm});
            skLineSegment(sketch, "E286.MirrorCS", {"start": v(-40.8, -14.75) * mm, "end": v(-43.42, -14.75) * mm});
            skLineSegment(sketch, "E287.MirrorCS", {"start": v(-43.42, -14.64) * mm, "end": v(-41.96, -13.18) * mm});
            skLineSegment(sketch, "E288.MirrorCS", {"start": v(-38, -25.84) * mm, "end": v(-36.54, -27.3) * mm});
            skLineSegment(sketch, "E289.MirrorCS", {"start": v(-54.5, -31.15) * mm, "end": v(-54.5, -29.52) * mm});
            skCircle(sketch, "E290.MirrorC", {"center": v(-46.3, -22.95) * mm, "radius": 2.1 * mm});
            skLineSegment(sketch, "E291.MirrorCS", {"start": v(-43.42, -31.15) * mm, "end": v(-40.8, -31.15) * mm});
            skLineSegment(sketch, "E292.MirrorCS", {"start": v(-51.22, -32.95) * mm, "end": v(-54.8, -32.95) * mm});
            skLineSegment(sketch, "E293.MirrorCS", {"start": v(-36.3, -27.86) * mm, "end": v(-36.3, -31.45) * mm});
            skLineSegment(sketch, "E294.MirrorCS", {"start": v(-40.8, -31.15) * mm, "end": v(-40.8, -29.5) * mm});
            skArc(sketch, "E295.MirrorCS", {"start": v(-36.3, -31.45) * mm, "mid": v(-36.75, -32.5) * mm, "end": v(-37.8, -32.95) * mm});
            skLineSegment(sketch, "E296.MirrorCS", {"start": v(-40.8, -29.5) * mm, "end": v(-43.97, -26.35) * mm});
            skLineSegment(sketch, "E297.MirrorCS", {"start": v(-43.97, -26.35) * mm, "end": v(-48.65, -26.35) * mm});
            skLineSegment(sketch, "E298.MirrorCS", {"start": v(-38.1, -29.52) * mm, "end": v(-38.1, -31.15) * mm});
            skLineSegment(sketch, "E299.MirrorCS", {"start": v(-54.5, -14.75) * mm, "end": v(-52.88, -14.75) * mm});
            skLineSegment(sketch, "E300.MirrorCS", {"start": v(-37.8, -32.95) * mm, "end": v(-41.4, -32.95) * mm});
            skLineSegment(sketch, "E301.MirrorCS", {"start": v(-48.65, -26.35) * mm, "end": v(-51.8, -29.5) * mm});
            skLineSegment(sketch, "E302.MirrorCS", {"start": v(-42.9, -25.29) * mm, "end": v(-39.75, -28.45) * mm});
            skLineSegment(sketch, "E303.MirrorCS", {"start": v(-38.1, -31.15) * mm, "end": v(-39.74, -31.15) * mm});
            skLineSegment(sketch, "E304.MirrorCS", {"start": v(-53.97, -29.52) * mm, "end": v(-52.88, -30.6) * mm});
            skLineSegment(sketch, "E305.MirrorCS", {"start": v(-39.74, -14.75) * mm, "end": v(-38.1, -14.75) * mm});
            skLineSegment(sketch, "E306.MirrorCS", {"start": v(-51.8, -29.5) * mm, "end": v(-51.8, -31.15) * mm});
            skLineSegment(sketch, "E307.MirrorCS", {"start": v(-38.65, -16.38) * mm, "end": v(-39.74, -15.29) * mm});
            skLineSegment(sketch, "E308.MirrorCS", {"start": v(-39.75, -28.45) * mm, "end": v(-38.1, -28.45) * mm});
            skLineSegment(sketch, "E309.MirrorCS", {"start": v(-38.1, -14.75) * mm, "end": v(-38.1, -16.38) * mm});
            skLineSegment(sketch, "E310.MirrorCS", {"start": v(-41.96, -32.72) * mm, "end": v(-43.42, -31.26) * mm});
            skLineSegment(sketch, "E311.MirrorCS", {"start": v(-51.8, -31.15) * mm, "end": v(-49.2, -31.15) * mm});
            skLineSegment(sketch, "E312.MirrorCS", {"start": v(-38.1, -28.45) * mm, "end": v(-38.1, -25.84) * mm});
            skLineSegment(sketch, "E313.MirrorCS", {"start": v(-39.74, -30.6) * mm, "end": v(-38.65, -29.52) * mm});
            skLineSegment(sketch, "E314.MirrorCS", {"start": v(-52.88, -31.15) * mm, "end": v(-54.5, -31.15) * mm});
            skLineSegment(sketch, "E315.MirrorCS", {"start": v(-54.5, -16.38) * mm, "end": v(-54.5, -14.75) * mm});
            skLineSegment(sketch, "E316.MirrorCS", {"start": v(-49.2, -31.26) * mm, "end": v(-50.66, -32.72) * mm});
            skLineSegment(sketch, "E317", {"start": v(-57.8, -12.95) * mm, "end": v(-54.8, -12.95) * mm});
            skLineSegment(sketch, "E318", {"start": v(-58.1, -17.45) * mm, "end": v(-54.5, -17.45) * mm});
            skLineSegment(sketch, "E319", {"start": v(-58.1, -28.45) * mm, "end": v(-54.5, -28.45) * mm});
            skLineSegment(sketch, "E320", {"start": v(-57.8, -32.95) * mm, "end": v(-54.8, -32.95) * mm});
            skArc(sketch, "E321", {"start": v(-58.27, -23.7) * mm, "mid": v(-56.3, -25.05) * mm, "end": v(-54.35, -23.7) * mm});
            skPoint(sketch, "E321.centerSnap0", {"position": v(-56.3, -17.45) * mm});
            skPoint(sketch, "E321.centerSnap1", {"position": v(-62.9, -22.95) * mm});
            skLineSegment(sketch, "E322.bottom", {"start": v(-49.7, -23.7) * mm, "end": v(-54.35, -23.7) * mm});
            skLineSegment(sketch, "E322.top", {"start": v(-49.7, -22.2) * mm, "end": v(-54.35, -22.2) * mm});
            skLineSegment(sketch, "E323.trimOffspring", {"start": v(-58.27, -22.2) * mm, "end": v(-62.9, -22.2) * mm});
            skLineSegment(sketch, "E324.trimOffspring", {"start": v(-58.27, -23.7) * mm, "end": v(-62.9, -23.7) * mm});
            skLineSegment(sketch, "E325.trimOffspring", {"start": v(-62.9, -22.2) * mm, "end": v(-62.9, -20.6) * mm});
            skLineSegment(sketch, "E326.trimOffspring", {"start": v(-49.7, -22.2) * mm, "end": v(-49.7, -20.6) * mm});
            skArc(sketch, "E327.trimOffspring", {"start": v(-54.35, -22.2) * mm, "mid": v(-56.3, -20.85) * mm, "end": v(-58.27, -22.2) * mm});
            skSolve(sketch);
        }
        {
            var Q0;
            Q0 = qSketchRegion(id + "F3", true);
            extrude(context, id + "F4", {"entities" : qUnion([Q0]), "depth" : 350 * mm});
        }
        {
            var Q0;
            Q0 = qSketchRegion(id + "F2", true);
            extrude(context, id + "F5", {"entities" : qUnion([Q0]), "depth" : 500 * mm});
        }
        {
            var Q0;
            Q0=qCreatedBy(makeId("Top.planeOp"),FACE);
            var sketch = newSketch(context, id + "F6", { "sketchPlane" : qUnion([Q0])});
            skLineSegment(sketch, "E328.bottom", {"start": v(206.27, 54.8) * mm, "end": v(420.27, 54.8) * mm});
            skLineSegment(sketch, "E328.top", {"start": v(206.27, -159.2) * mm, "end": v(420.27, -159.2) * mm});
            skLineSegment(sketch, "E328.left", {"start": v(206.27, 54.8) * mm, "end": v(206.27, -159.2) * mm});
            skLineSegment(sketch, "E328.right", {"start": v(420.27, 54.8) * mm, "end": v(420.27, -159.2) * mm});
            skLineSegment(sketch, "E329.bottom", {"start": v(417.77, -156.7) * mm, "end": v(208.77, -156.7) * mm, "construction": true});
            skLineSegment(sketch, "E329.top", {"start": v(417.77, 52.3) * mm, "end": v(208.77, 52.3) * mm, "construction": true});
            skLineSegment(sketch, "E329.left", {"start": v(417.77, -156.7) * mm, "end": v(417.77, 52.3) * mm, "construction": true});
            skLineSegment(sketch, "E329.right", {"start": v(208.77, -156.7) * mm, "end": v(208.77, 52.3) * mm, "construction": true});
            skPoint(sketch, "E329.middle", {"position": v(313.27, -52.2) * mm});
            skPoint(sketch, "E329.middle.positionSnap0", {"position": v(206.27, -52.2) * mm});
            skPoint(sketch, "E329.middle.positionSnap1", {"position": v(313.27, 54.8) * mm});
            skPoint(sketch, "E329.centerSnap0", {"position": v(206.27, -52.2) * mm});
            skPoint(sketch, "E329.centerSnap1", {"position": v(313.27, 54.8) * mm});
            skCircle(sketch, "E330", {"center": v(417.77, 52.3) * mm, "radius": 1.5 * mm});
            skCircle(sketch, "E331", {"center": v(208.77, 52.3) * mm, "radius": 1.5 * mm});
            skCircle(sketch, "E332", {"center": v(208.77, -156.7) * mm, "radius": 1.5 * mm});
            skCircle(sketch, "E333", {"center": v(417.77, -156.7) * mm, "radius": 1.5 * mm});
            skSolve(sketch);
        }
        {
            var Q0;
            Q0 = qSketchRegion(id + "F6", true);
            extrude(context, id + "F7", {"entities" : qUnion([Q0]), "depth" : 3 * mm});
        }
        {
            var Q0;
            Q0 = qSketchRegion(id + "F0", true);
            extrude(context, id + "F8", {"entities" : qUnion([Q0]), "depth" : 350 * mm});
        }
        {
            var Q0;
            Q0=qCreatedBy(makeId("Top.planeOp"),FACE);
            var sketch = newSketch(context, id + "F9", { "sketchPlane" : qUnion([Q0])});
            skLineSegment(sketch, "E334.bottom", {"start": v(792.13, 52.85) * mm, "end": v(815.41, 52.85) * mm});
            skLineSegment(sketch, "E334.top", {"start": v(792.13, -251.95) * mm, "end": v(815.41, -251.95) * mm});
            skLineSegment(sketch, "E334.left", {"start": v(787.13, 47.85) * mm, "end": v(787.13, 24.57) * mm});
            skLineSegment(sketch, "E334.right", {"start": v(1091.93, 47.85) * mm, "end": v(1091.93, 24.57) * mm});
            skLineSegment(sketch, "E335.bottom", {"start": v(1087.17, -247.18) * mm, "end": v(791.9, -247.18) * mm, "construction": true});
            skLineSegment(sketch, "E335.top", {"start": v(1087.17, 48.1) * mm, "end": v(791.9, 48.1) * mm, "construction": true});
            skLineSegment(sketch, "E335.left", {"start": v(1087.17, -247.18) * mm, "end": v(1087.17, 48.1) * mm, "construction": true});
            skLineSegment(sketch, "E335.right", {"start": v(791.9, -247.18) * mm, "end": v(791.9, 48.1) * mm, "construction": true});
            skPoint(sketch, "E335.middle", {"position": v(939.53, -99.55) * mm});
            skPoint(sketch, "E335.middle.positionSnap0", {"position": v(787.13, -99.55) * mm});
            skPoint(sketch, "E335.middle.positionSnap1", {"position": v(939.53, 52.85) * mm});
            skPoint(sketch, "E335.centerSnap0", {"position": v(787.13, -99.55) * mm});
            skPoint(sketch, "E335.centerSnap1", {"position": v(939.53, 52.85) * mm});
            skCircle(sketch, "E336", {"center": v(1087.17, 48.1) * mm, "radius": 2 * mm});
            skCircle(sketch, "E337", {"center": v(791.9, 48.1) * mm, "radius": 2 * mm});
            skCircle(sketch, "E338", {"center": v(791.9, -247.18) * mm, "radius": 2 * mm});
            skCircle(sketch, "E339", {"center": v(1087.17, -247.18) * mm, "radius": 2 * mm});
            skPoint(sketch, "E340.visualSharp", {"position": v(787.13, -251.95) * mm});
            skArc(sketch, "E340.filletArc", {"start": v(787.13, -246.95) * mm, "mid": v(788.6, -250.48) * mm, "end": v(792.13, -251.95) * mm});
            skPoint(sketch, "E341.visualSharp", {"position": v(1091.93, -251.95) * mm});
            skArc(sketch, "E341.filletArc", {"start": v(1086.93, -251.95) * mm, "mid": v(1090.46, -250.48) * mm, "end": v(1091.93, -246.95) * mm});
            skPoint(sketch, "E342.visualSharp", {"position": v(1091.93, 52.85) * mm});
            skArc(sketch, "E342.filletArc", {"start": v(1091.93, 47.85) * mm, "mid": v(1090.46, 51.39) * mm, "end": v(1086.93, 52.85) * mm});
            skPoint(sketch, "E343.visualSharp", {"position": v(787.13, 52.85) * mm});
            skArc(sketch, "E343.filletArc", {"start": v(792.13, 52.85) * mm, "mid": v(788.6, 51.39) * mm, "end": v(787.13, 47.85) * mm});
            skLineSegment(sketch, "E344", {"start": v(1091.93, -246.95) * mm, "end": v(1091.93, -251.95) * mm});
            skLineSegment(sketch, "E345", {"start": v(1086.93, -251.95) * mm, "end": v(1091.93, -251.95) * mm});
            skLineSegment(sketch, "E346", {"start": v(787.13, -246.95) * mm, "end": v(787.13, -251.95) * mm});
            skLineSegment(sketch, "E347", {"start": v(787.13, -251.95) * mm, "end": v(792.13, -251.95) * mm});
            skLineSegment(sketch, "E348", {"start": v(792.13, 52.85) * mm, "end": v(787.13, 52.85) * mm});
            skLineSegment(sketch, "E349", {"start": v(787.13, 52.85) * mm, "end": v(787.13, 47.85) * mm});
            skLineSegment(sketch, "E350", {"start": v(1086.93, 52.85) * mm, "end": v(1091.93, 52.85) * mm});
            skLineSegment(sketch, "E351", {"start": v(1091.93, 52.85) * mm, "end": v(1091.93, 47.85) * mm});
            skLineSegment(sketch, "E352.bottom", {"start": v(1082.4, -242.42) * mm, "end": v(796.65, -242.42) * mm});
            skLineSegment(sketch, "E352.top", {"start": v(1082.4, 43.33) * mm, "end": v(796.65, 43.33) * mm});
            skLineSegment(sketch, "E352.left", {"start": v(1082.4, -242.42) * mm, "end": v(1082.4, 43.33) * mm});
            skLineSegment(sketch, "E352.right", {"start": v(796.65, -242.42) * mm, "end": v(796.65, 43.33) * mm});
            skLineSegment(sketch, "E353.bottom", {"start": v(1016.02, -204.32) * mm, "end": v(863.04, -204.32) * mm});
            skLineSegment(sketch, "E353.top", {"start": v(1016.02, 5.23) * mm, "end": v(863.04, 5.23) * mm});
            skLineSegment(sketch, "E353.left", {"start": v(1044.3, -176.04) * mm, "end": v(1044.3, -23.06) * mm});
            skLineSegment(sketch, "E353.right", {"start": v(834.75, -176.04) * mm, "end": v(834.75, -23.06) * mm});
            skLineSegment(sketch, "E354", {"start": v(1091.93, 52.85) * mm, "end": v(787.13, -251.95) * mm, "construction": true});
            skLineSegment(sketch, "E355", {"start": v(787.13, 52.85) * mm, "end": v(1091.93, -251.95) * mm, "construction": true});
            skLineSegment(sketch, "E356", {"start": v(971.26, -131.28) * mm, "end": v(985.4, -117.13) * mm, "construction": true});
            skLineSegment(sketch, "E357", {"start": v(902.97, -136.1) * mm, "end": v(917.12, -150.24) * mm, "construction": true});
            skLineSegment(sketch, "E358", {"start": v(917.12, -150.24) * mm, "end": v(1082.4, 15.04) * mm, "construction": true});
            skLineSegment(sketch, "E359", {"start": v(985.4, -117.13) * mm, "end": v(824.94, 43.33) * mm, "construction": true});
            skLineSegment(sketch, "E360", {"start": v(917.12, -150.24) * mm, "end": v(824.94, -242.42) * mm, "construction": true});
            skLineSegment(sketch, "E361", {"start": v(985.4, -117.13) * mm, "end": v(1082.4, -214.14) * mm, "construction": true});
            skLineSegment(sketch, "E362.MirrorCS", {"start": v(957.12, -145.42) * mm, "end": v(796.65, 15.04) * mm, "construction": true});
            skLineSegment(sketch, "E363.MirrorCS", {"start": v(957.12, -145.42) * mm, "end": v(1054.12, -242.42) * mm, "construction": true});
            skLineSegment(sketch, "E364.MirrorCS", {"start": v(888.83, -121.96) * mm, "end": v(796.65, -214.14) * mm, "construction": true});
            skLineSegment(sketch, "E365.MirrorCS", {"start": v(888.83, -121.96) * mm, "end": v(1054.12, 43.33) * mm, "construction": true});
            skLineSegment(sketch, "E366", {"start": v(796.65, -214.14) * mm, "end": v(787.13, -223.66) * mm});
            skLineSegment(sketch, "E367", {"start": v(824.94, -242.42) * mm, "end": v(815.41, -251.95) * mm});
            skLineSegment(sketch, "E368", {"start": v(1054.12, -242.42) * mm, "end": v(1063.64, -251.95) * mm});
            skLineSegment(sketch, "E369", {"start": v(1082.4, -214.14) * mm, "end": v(1091.93, -223.66) * mm});
            skLineSegment(sketch, "E370", {"start": v(1054.12, 43.33) * mm, "end": v(1063.64, 52.85) * mm});
            skLineSegment(sketch, "E371", {"start": v(1082.4, 15.04) * mm, "end": v(1091.93, 24.57) * mm});
            skLineSegment(sketch, "E372", {"start": v(824.94, 43.33) * mm, "end": v(815.41, 52.85) * mm});
            skLineSegment(sketch, "E373", {"start": v(796.65, 15.04) * mm, "end": v(787.13, 24.57) * mm});
            skLineSegment(sketch, "E374.trimOffspring", {"start": v(1063.64, 52.85) * mm, "end": v(1086.93, 52.85) * mm});
            skLineSegment(sketch, "E375.trimOffspring", {"start": v(787.13, -223.66) * mm, "end": v(787.13, -246.95) * mm});
            skLineSegment(sketch, "E376.trimOffspring", {"start": v(1091.93, -223.66) * mm, "end": v(1091.93, -246.95) * mm});
            skLineSegment(sketch, "E377.trimOffspring", {"start": v(1063.64, -251.95) * mm, "end": v(1086.93, -251.95) * mm});
            skLineSegment(sketch, "E378", {"start": v(834.75, -104.5) * mm, "end": v(809.35, -104.5) * mm, "construction": true});
            skLineSegment(sketch, "E379", {"start": v(809.35, -104.5) * mm, "end": v(809.35, 2.34) * mm});
            skLineSegment(sketch, "E380", {"start": v(809.35, -104.5) * mm, "end": v(809.35, -201.44) * mm});
            skLineSegment(sketch, "E381", {"start": v(809.35, -201.44) * mm, "end": v(834.75, -176.04) * mm});
            skLineSegment(sketch, "E382", {"start": v(809.35, 2.34) * mm, "end": v(834.75, -23.06) * mm});
            skLineSegment(sketch, "E383", {"start": v(939.53, 52.85) * mm, "end": v(939.53, -247.18) * mm, "construction": true});
            skLineSegment(sketch, "E384", {"start": v(787.13, -99.55) * mm, "end": v(1082.4, -99.55) * mm, "construction": true});
            skLineSegment(sketch, "E385.MirrorCS", {"start": v(1069.7, -104.5) * mm, "end": v(1069.7, 2.34) * mm});
            skLineSegment(sketch, "E386.MirrorCS", {"start": v(1069.7, -104.5) * mm, "end": v(1069.7, -201.44) * mm});
            skLineSegment(sketch, "E387", {"start": v(1069.7, 2.34) * mm, "end": v(1044.3, -23.06) * mm});
            skLineSegment(sketch, "E388", {"start": v(1069.7, -201.44) * mm, "end": v(1044.3, -176.04) * mm});
            skLineSegment(sketch, "E389", {"start": v(931.5, -204.32) * mm, "end": v(931.5, -229.72) * mm, "construction": true});
            skLineSegment(sketch, "E390", {"start": v(931.5, -229.72) * mm, "end": v(837.64, -229.72) * mm});
            skLineSegment(sketch, "E391", {"start": v(837.64, -229.72) * mm, "end": v(863.04, -204.32) * mm});
            skLineSegment(sketch, "E392", {"start": v(931.5, -229.72) * mm, "end": v(1041.42, -229.72) * mm});
            skLineSegment(sketch, "E393", {"start": v(1041.42, -229.72) * mm, "end": v(1016.02, -204.32) * mm});
            skLineSegment(sketch, "E394.MirrorCS", {"start": v(931.5, 30.63) * mm, "end": v(837.64, 30.63) * mm});
            skLineSegment(sketch, "E395.MirrorCS", {"start": v(931.5, 30.63) * mm, "end": v(1041.42, 30.63) * mm});
            skLineSegment(sketch, "E396", {"start": v(837.64, 30.63) * mm, "end": v(863.04, 5.23) * mm});
            skLineSegment(sketch, "E397", {"start": v(1041.42, 30.63) * mm, "end": v(1016.02, 5.23) * mm});
            skPoint(sketch, "E398.orphan", {"position": v(834.75, 5.23) * mm});
            skPoint(sketch, "E399.orphan", {"position": v(1044.3, 5.23) * mm});
            skPoint(sketch, "E400.orphan", {"position": v(1044.3, -204.32) * mm});
            skPoint(sketch, "E401.orphan", {"position": v(834.75, -204.32) * mm});
            skSolve(sketch);
        }
        {
            var Q0;
            Q0 = qSketchRegion(id + "F9", true);
            extrude(context, id + "F10", {"entities" : qUnion([Q0]), "depth" : 3 * mm});
        }
        {
            var Q0;
            Q0 = qSketchRegion(id + "F1", true);
            extrude(context, id + "F11", {"entities" : qUnion([Q0]), "depth" : 335 * mm});
        }
        {
            var Q0;
            Q0=qCreatedBy(makeId("Top.planeOp"),FACE);
            var sketch = newSketch(context, id + "F12", { "sketchPlane" : qUnion([Q0])});
            skCircle(sketch, "E402", {"center": v(43.85, -54.2) * mm, "radius": 4 * mm});
            skSolve(sketch);
        }
        {
            var Q0;
            Q0 = qSketchRegion(id + "F12", true);
            extrude(context, id + "F13", {"entities" : qUnion([Q0]), "depth" : 365 * mm});
        }
        {
            var Q0;
            Q0=qCreatedBy(makeId("Top.planeOp"),FACE);
            var sketch = newSketch(context, id + "F14", { "sketchPlane" : qUnion([Q0])});
            skLineSegment(sketch, "E403.bottom", {"start": v(-26.94, -249.07) * mm, "end": v(0, -249.07) * mm});
            skLineSegment(sketch, "E403.top", {"start": v(-26.94, -264.48) * mm, "end": v(0, -264.48) * mm});
            skLineSegment(sketch, "E403.left", {"start": v(-26.94, -249.07) * mm, "end": v(-26.94, -264.48) * mm});
            skLineSegment(sketch, "E403.right", {"start": v(0, -249.07) * mm, "end": v(0, -264.48) * mm});
            skSolve(sketch);
        }
        {
            var Q0;
            Q0 = qSketchRegion(id + "F14", true);
            extrude(context, id + "F15", {"entities" : qUnion([Q0]), "depth" : 80 * mm});
        }
        {
            var Q0;
            Q0=qCreatedBy(makeId("Top.planeOp"),FACE);
            var sketch = newSketch(context, id + "F16", { "sketchPlane" : qUnion([Q0])});
            skArc(sketch, "E404.0", {"start": v(78.69, 49.3) * mm, "mid": v(77.63, 48.85) * mm, "end": v(77.19, 47.8) * mm});
            skLineSegment(sketch, "E405.0", {"start": v(77.19, 47.8) * mm, "end": v(77.19, 44.2) * mm});
            skLineSegment(sketch, "E406.0", {"start": v(80.62, 47.5) * mm, "end": v(78.99, 47.5) * mm});
            skLineSegment(sketch, "E407.0", {"start": v(80.62, 46.95) * mm, "end": v(80.62, 47.5) * mm});
            skLineSegment(sketch, "E408.0", {"start": v(79.53, 45.86) * mm, "end": v(80.62, 46.95) * mm});
            skLineSegment(sketch, "E409.0", {"start": v(78.99, 45.86) * mm, "end": v(79.53, 45.86) * mm});
            skLineSegment(sketch, "E410.0", {"start": v(78.99, 47.5) * mm, "end": v(78.99, 45.86) * mm});
            skArc(sketch, "E411.0", {"start": v(82.84, 49.06) * mm, "mid": v(82.58, 49.23) * mm, "end": v(82.28, 49.3) * mm});
            skLineSegment(sketch, "E412.0", {"start": v(82.28, 49.3) * mm, "end": v(78.69, 49.3) * mm});
            skLineSegment(sketch, "E413.0", {"start": v(81.69, 45.85) * mm, "end": v(81.69, 47.5) * mm});
            skLineSegment(sketch, "E414.0", {"start": v(81.69, 47.5) * mm, "end": v(84.3, 47.5) * mm});
            skLineSegment(sketch, "E415.0", {"start": v(84.3, 47.6) * mm, "end": v(82.84, 49.06) * mm});
            skLineSegment(sketch, "E416.0", {"start": v(84.3, 47.5) * mm, "end": v(84.3, 47.6) * mm});
            skLineSegment(sketch, "E417.0", {"start": v(84.85, 42.7) * mm, "end": v(81.69, 45.85) * mm});
            skLineSegment(sketch, "E418.0", {"start": v(80.63, 44.8) * mm, "end": v(83.79, 41.63) * mm});
            skLineSegment(sketch, "E419.0", {"start": v(78.99, 44.8) * mm, "end": v(80.63, 44.8) * mm});
            skArc(sketch, "E420.0", {"start": v(77.19, 44.2) * mm, "mid": v(77.25, 43.9) * mm, "end": v(77.42, 43.64) * mm});
            skLineSegment(sketch, "E421.0", {"start": v(77.42, 43.64) * mm, "end": v(78.88, 42.18) * mm});
            skLineSegment(sketch, "E422.0", {"start": v(78.88, 42.18) * mm, "end": v(78.99, 42.18) * mm});
            skLineSegment(sketch, "E423.0", {"start": v(78.99, 42.18) * mm, "end": v(78.99, 44.8) * mm});
            skLineSegment(sketch, "E424.0", {"start": v(83.79, 41.63) * mm, "end": v(83.79, 36.95) * mm});
            skLineSegment(sketch, "E425.0", {"start": v(89.53, 42.7) * mm, "end": v(84.85, 42.7) * mm});
            skCircle(sketch, "E426.0", {"center": v(87.19, 39.3) * mm, "radius": 2.1 * mm});
            skLineSegment(sketch, "E427.0", {"start": v(91.54, 49.06) * mm, "end": v(90.08, 47.6) * mm});
            skLineSegment(sketch, "E428.0", {"start": v(90.08, 47.5) * mm, "end": v(92.69, 47.5) * mm});
            skLineSegment(sketch, "E429.0", {"start": v(92.69, 47.5) * mm, "end": v(92.69, 45.85) * mm});
            skLineSegment(sketch, "E430.0", {"start": v(92.69, 45.85) * mm, "end": v(89.53, 42.7) * mm});
            skLineSegment(sketch, "E431.0", {"start": v(90.59, 41.63) * mm, "end": v(93.75, 44.8) * mm});
            skLineSegment(sketch, "E432.0", {"start": v(93.75, 44.8) * mm, "end": v(95.39, 44.8) * mm});
            skLineSegment(sketch, "E433.0", {"start": v(95.39, 44.8) * mm, "end": v(95.39, 42.18) * mm});
            skLineSegment(sketch, "E434.0", {"start": v(95.39, 45.86) * mm, "end": v(95.39, 47.5) * mm});
            skLineSegment(sketch, "E435.0", {"start": v(94.85, 45.86) * mm, "end": v(95.39, 45.86) * mm});
            skLineSegment(sketch, "E436.0", {"start": v(93.76, 46.95) * mm, "end": v(94.85, 45.86) * mm});
            skLineSegment(sketch, "E437.0", {"start": v(93.76, 47.5) * mm, "end": v(93.76, 46.95) * mm});
            skLineSegment(sketch, "E438.0", {"start": v(95.39, 47.5) * mm, "end": v(93.76, 47.5) * mm});
            skArc(sketch, "E439.0", {"start": v(92.1, 49.3) * mm, "mid": v(91.8, 49.23) * mm, "end": v(91.54, 49.06) * mm});
            skLineSegment(sketch, "E440.0", {"start": v(95.69, 49.3) * mm, "end": v(92.1, 49.3) * mm});
            skArc(sketch, "E441.0", {"start": v(97.19, 47.8) * mm, "mid": v(96.75, 48.85) * mm, "end": v(95.69, 49.3) * mm});
            skLineSegment(sketch, "E442.0", {"start": v(97.19, 44.2) * mm, "end": v(97.19, 47.8) * mm});
            skArc(sketch, "E443.0", {"start": v(96.96, 43.64) * mm, "mid": v(97.13, 43.9) * mm, "end": v(97.19, 44.2) * mm});
            skLineSegment(sketch, "E444.0", {"start": v(95.5, 42.18) * mm, "end": v(96.96, 43.64) * mm});
            skLineSegment(sketch, "E445.0", {"start": v(95.39, 42.18) * mm, "end": v(95.5, 42.18) * mm});
            skLineSegment(sketch, "E446.0", {"start": v(90.59, 36.95) * mm, "end": v(90.59, 41.63) * mm});
            skLineSegment(sketch, "E447.0", {"start": v(93.75, 33.8) * mm, "end": v(90.59, 36.95) * mm});
            skLineSegment(sketch, "E448.0", {"start": v(95.39, 33.8) * mm, "end": v(93.75, 33.8) * mm});
            skLineSegment(sketch, "E449.0", {"start": v(95.39, 36.4) * mm, "end": v(95.39, 33.8) * mm});
            skLineSegment(sketch, "E450.0", {"start": v(95.5, 36.4) * mm, "end": v(95.39, 36.4) * mm});
            skLineSegment(sketch, "E451.0", {"start": v(96.96, 34.94) * mm, "end": v(95.5, 36.4) * mm});
            skArc(sketch, "E452.0", {"start": v(97.19, 34.39) * mm, "mid": v(97.13, 34.69) * mm, "end": v(96.96, 34.94) * mm});
            skLineSegment(sketch, "E453.0", {"start": v(97.19, 30.8) * mm, "end": v(97.19, 34.39) * mm});
            skLineSegment(sketch, "E454.0", {"start": v(95.39, 32.72) * mm, "end": v(94.85, 32.72) * mm});
            skLineSegment(sketch, "E455.0", {"start": v(94.85, 32.72) * mm, "end": v(93.76, 31.63) * mm});
            skLineSegment(sketch, "E456.0", {"start": v(93.76, 31.63) * mm, "end": v(93.76, 31.1) * mm});
            skLineSegment(sketch, "E457.0", {"start": v(93.76, 31.1) * mm, "end": v(95.39, 31.1) * mm});
            skLineSegment(sketch, "E458.0", {"start": v(95.39, 31.1) * mm, "end": v(95.39, 32.72) * mm});
            skArc(sketch, "E459.0", {"start": v(95.69, 29.3) * mm, "mid": v(96.75, 29.73) * mm, "end": v(97.19, 30.8) * mm});
            skLineSegment(sketch, "E460.0.2", {"start": v(83.79, 36.95) * mm, "end": v(80.63, 33.8) * mm});
            skLineSegment(sketch, "E460.0.3", {"start": v(80.63, 33.8) * mm, "end": v(78.99, 33.8) * mm});
            skLineSegment(sketch, "E460.0.4", {"start": v(78.99, 33.8) * mm, "end": v(78.99, 36.4) * mm});
            skLineSegment(sketch, "E460.0.5", {"start": v(78.99, 36.4) * mm, "end": v(78.88, 36.4) * mm});
            skLineSegment(sketch, "E460.0.6", {"start": v(78.88, 36.4) * mm, "end": v(77.42, 34.94) * mm});
            skArc(sketch, "E460.0.7", {"start": v(77.42, 34.94) * mm, "mid": v(77.25, 34.69) * mm, "end": v(77.19, 34.39) * mm});
            skLineSegment(sketch, "E460.0.8", {"start": v(77.19, 34.39) * mm, "end": v(77.19, 30.8) * mm});
            skArc(sketch, "E460.0.9", {"start": v(77.19, 30.8) * mm, "mid": v(77.63, 29.73) * mm, "end": v(78.69, 29.3) * mm});
            skLineSegment(sketch, "E460.0.10", {"start": v(78.69, 29.3) * mm, "end": v(82.28, 29.3) * mm});
            skArc(sketch, "E460.0.11", {"start": v(82.28, 29.3) * mm, "mid": v(82.58, 29.35) * mm, "end": v(82.84, 29.52) * mm});
            skLineSegment(sketch, "E460.0.12", {"start": v(82.84, 29.52) * mm, "end": v(84.3, 30.98) * mm});
            skLineSegment(sketch, "E460.0.13", {"start": v(84.3, 30.98) * mm, "end": v(84.3, 31.1) * mm});
            skLineSegment(sketch, "E460.0.14", {"start": v(84.3, 31.1) * mm, "end": v(81.69, 31.1) * mm});
            skLineSegment(sketch, "E460.0.15", {"start": v(81.69, 31.1) * mm, "end": v(81.69, 32.73) * mm});
            skLineSegment(sketch, "E460.0.16", {"start": v(81.69, 32.73) * mm, "end": v(84.85, 35.9) * mm});
            skLineSegment(sketch, "E460.0.17", {"start": v(84.85, 35.9) * mm, "end": v(89.53, 35.9) * mm});
            skLineSegment(sketch, "E460.0.18", {"start": v(89.53, 35.9) * mm, "end": v(92.69, 32.73) * mm});
            skLineSegment(sketch, "E460.0.19", {"start": v(92.69, 32.73) * mm, "end": v(92.69, 31.1) * mm});
            skLineSegment(sketch, "E460.0.20", {"start": v(92.69, 31.1) * mm, "end": v(90.08, 31.1) * mm});
            skLineSegment(sketch, "E460.0.21", {"start": v(90.08, 31.1) * mm, "end": v(90.08, 30.98) * mm});
            skLineSegment(sketch, "E460.0.22", {"start": v(90.08, 30.98) * mm, "end": v(91.54, 29.52) * mm});
            skArc(sketch, "E460.0.23", {"start": v(91.54, 29.52) * mm, "mid": v(91.8, 29.35) * mm, "end": v(92.1, 29.3) * mm});
            skLineSegment(sketch, "E460.0.24", {"start": v(92.1, 29.3) * mm, "end": v(95.69, 29.3) * mm});
            skLineSegment(sketch, "E460.0.45", {"start": v(90.08, 47.6) * mm, "end": v(90.08, 47.5) * mm});
            skLineSegment(sketch, "E461.0", {"start": v(79.53, 32.72) * mm, "end": v(78.99, 32.72) * mm});
            skLineSegment(sketch, "E462.0", {"start": v(78.99, 32.72) * mm, "end": v(78.99, 31.1) * mm});
            skLineSegment(sketch, "E463.0", {"start": v(78.99, 31.1) * mm, "end": v(80.62, 31.1) * mm});
            skLineSegment(sketch, "E464.0", {"start": v(80.62, 31.1) * mm, "end": v(80.62, 31.63) * mm});
            skLineSegment(sketch, "E465.0", {"start": v(80.62, 31.63) * mm, "end": v(79.53, 32.72) * mm});
            skSolve(sketch);
        }
        {
            var Q0;
            Q0 = qSketchRegion(id + "F16", true);
            extrude(context, id + "F17", {"entities" : qUnion([Q0]), "depth" : 300 * mm, "offsetDistance" : 25 * mm});
        }
        {
            var Q0;
            Q0=qCreatedBy(makeId("Top.planeOp"),FACE);
            var sketch = newSketch(context, id + "F18", { "sketchPlane" : qUnion([Q0])});
            skArc(sketch, "E466.0", {"start": v(110.25, 50) * mm, "mid": v(109.2, 49.57) * mm, "end": v(108.75, 48.5) * mm});
            skLineSegment(sketch, "E467.0", {"start": v(108.75, 48.5) * mm, "end": v(108.75, 44.92) * mm});
            skLineSegment(sketch, "E468.0", {"start": v(112.18, 48.2) * mm, "end": v(110.55, 48.2) * mm});
            skLineSegment(sketch, "E469.0", {"start": v(112.18, 47.67) * mm, "end": v(112.18, 48.2) * mm});
            skLineSegment(sketch, "E470.0", {"start": v(111.1, 46.58) * mm, "end": v(112.18, 47.67) * mm});
            skLineSegment(sketch, "E471.0", {"start": v(110.55, 46.58) * mm, "end": v(111.1, 46.58) * mm});
            skLineSegment(sketch, "E472.0", {"start": v(110.55, 48.2) * mm, "end": v(110.55, 46.58) * mm});
            skArc(sketch, "E473.0", {"start": v(114.4, 49.78) * mm, "mid": v(114.15, 49.95) * mm, "end": v(113.84, 50) * mm});
            skLineSegment(sketch, "E474.0", {"start": v(113.84, 50) * mm, "end": v(110.25, 50) * mm});
            skLineSegment(sketch, "E475.0", {"start": v(113.25, 46.57) * mm, "end": v(113.25, 48.2) * mm});
            skLineSegment(sketch, "E476.0", {"start": v(113.25, 48.2) * mm, "end": v(115.86, 48.2) * mm});
            skLineSegment(sketch, "E477.0", {"start": v(115.86, 48.32) * mm, "end": v(114.4, 49.78) * mm});
            skLineSegment(sketch, "E478.0", {"start": v(115.86, 48.2) * mm, "end": v(115.86, 48.32) * mm});
            skLineSegment(sketch, "E479.0", {"start": v(116.41, 43.4) * mm, "end": v(113.25, 46.57) * mm});
            skLineSegment(sketch, "E480.0", {"start": v(112.2, 45.5) * mm, "end": v(115.35, 42.35) * mm});
            skLineSegment(sketch, "E481.0", {"start": v(110.55, 45.5) * mm, "end": v(112.2, 45.5) * mm});
            skArc(sketch, "E482.0", {"start": v(108.75, 44.92) * mm, "mid": v(108.81, 44.61) * mm, "end": v(108.98, 44.36) * mm});
            skLineSegment(sketch, "E483.0", {"start": v(108.98, 44.36) * mm, "end": v(110.44, 42.9) * mm});
            skLineSegment(sketch, "E484.0", {"start": v(110.44, 42.9) * mm, "end": v(110.55, 42.9) * mm});
            skLineSegment(sketch, "E485.0", {"start": v(110.55, 42.9) * mm, "end": v(110.55, 45.5) * mm});
            skLineSegment(sketch, "E486.0", {"start": v(115.35, 42.35) * mm, "end": v(115.35, 37.67) * mm});
            skLineSegment(sketch, "E487.0", {"start": v(121.1, 43.4) * mm, "end": v(116.41, 43.4) * mm});
            skCircle(sketch, "E488.0", {"center": v(118.75, 40) * mm, "radius": 2.1 * mm});
            skLineSegment(sketch, "E489.0", {"start": v(123.1, 49.78) * mm, "end": v(121.64, 48.32) * mm});
            skLineSegment(sketch, "E490.0", {"start": v(121.64, 48.2) * mm, "end": v(124.25, 48.2) * mm});
            skLineSegment(sketch, "E491.0", {"start": v(124.25, 48.2) * mm, "end": v(124.25, 46.57) * mm});
            skLineSegment(sketch, "E492.0", {"start": v(124.25, 46.57) * mm, "end": v(121.1, 43.4) * mm});
            skLineSegment(sketch, "E493.0", {"start": v(122.15, 42.35) * mm, "end": v(125.31, 45.5) * mm});
            skLineSegment(sketch, "E494.0", {"start": v(125.31, 45.5) * mm, "end": v(126.95, 45.5) * mm});
            skLineSegment(sketch, "E495.0", {"start": v(126.95, 45.5) * mm, "end": v(126.95, 42.9) * mm});
            skLineSegment(sketch, "E496.0", {"start": v(126.95, 46.58) * mm, "end": v(126.95, 48.2) * mm});
            skLineSegment(sketch, "E497.0", {"start": v(126.41, 46.58) * mm, "end": v(126.95, 46.58) * mm});
            skLineSegment(sketch, "E498.0", {"start": v(125.32, 47.67) * mm, "end": v(126.41, 46.58) * mm});
            skLineSegment(sketch, "E499.0", {"start": v(125.32, 48.2) * mm, "end": v(125.32, 47.67) * mm});
            skLineSegment(sketch, "E500.0", {"start": v(126.95, 48.2) * mm, "end": v(125.32, 48.2) * mm});
            skArc(sketch, "E501.0", {"start": v(123.66, 50) * mm, "mid": v(123.36, 49.95) * mm, "end": v(123.1, 49.78) * mm});
            skLineSegment(sketch, "E502.0", {"start": v(127.25, 50) * mm, "end": v(123.66, 50) * mm});
            skArc(sketch, "E503.0", {"start": v(128.75, 48.5) * mm, "mid": v(128.31, 49.57) * mm, "end": v(127.25, 50) * mm});
            skLineSegment(sketch, "E504.0", {"start": v(128.75, 44.92) * mm, "end": v(128.75, 48.5) * mm});
            skArc(sketch, "E505.0", {"start": v(128.52, 44.36) * mm, "mid": v(128.7, 44.61) * mm, "end": v(128.75, 44.92) * mm});
            skLineSegment(sketch, "E506.0", {"start": v(127.06, 42.9) * mm, "end": v(128.52, 44.36) * mm});
            skLineSegment(sketch, "E507.0", {"start": v(126.95, 42.9) * mm, "end": v(127.06, 42.9) * mm});
            skLineSegment(sketch, "E508.0", {"start": v(122.15, 37.67) * mm, "end": v(122.15, 42.35) * mm});
            skLineSegment(sketch, "E509.0", {"start": v(125.31, 34.5) * mm, "end": v(122.15, 37.67) * mm});
            skLineSegment(sketch, "E510.0", {"start": v(126.95, 34.5) * mm, "end": v(125.31, 34.5) * mm});
            skLineSegment(sketch, "E511.0", {"start": v(126.95, 37.12) * mm, "end": v(126.95, 34.5) * mm});
            skLineSegment(sketch, "E512.0", {"start": v(127.06, 37.12) * mm, "end": v(126.95, 37.12) * mm});
            skLineSegment(sketch, "E513.0", {"start": v(128.52, 35.66) * mm, "end": v(127.06, 37.12) * mm});
            skArc(sketch, "E514.0", {"start": v(128.75, 35.1) * mm, "mid": v(128.7, 35.4) * mm, "end": v(128.52, 35.66) * mm});
            skLineSegment(sketch, "E515.0", {"start": v(128.75, 31.5) * mm, "end": v(128.75, 35.1) * mm});
            skLineSegment(sketch, "E516.0", {"start": v(126.95, 33.44) * mm, "end": v(126.41, 33.44) * mm});
            skLineSegment(sketch, "E517.0", {"start": v(126.41, 33.44) * mm, "end": v(125.32, 32.35) * mm});
            skLineSegment(sketch, "E518.0", {"start": v(125.32, 32.35) * mm, "end": v(125.32, 31.8) * mm});
            skLineSegment(sketch, "E519.0", {"start": v(125.32, 31.8) * mm, "end": v(126.95, 31.8) * mm});
            skLineSegment(sketch, "E520.0", {"start": v(126.95, 31.8) * mm, "end": v(126.95, 33.44) * mm});
            skArc(sketch, "E521.0", {"start": v(127.25, 30) * mm, "mid": v(128.31, 30.45) * mm, "end": v(128.75, 31.5) * mm});
            skLineSegment(sketch, "E522.0.2", {"start": v(115.35, 37.67) * mm, "end": v(112.2, 34.5) * mm});
            skLineSegment(sketch, "E522.0.3", {"start": v(112.2, 34.5) * mm, "end": v(110.55, 34.5) * mm});
            skLineSegment(sketch, "E522.0.4", {"start": v(110.55, 34.5) * mm, "end": v(110.55, 37.12) * mm});
            skLineSegment(sketch, "E522.0.5", {"start": v(110.55, 37.12) * mm, "end": v(110.44, 37.12) * mm});
            skLineSegment(sketch, "E522.0.6", {"start": v(110.44, 37.12) * mm, "end": v(108.98, 35.66) * mm});
            skArc(sketch, "E522.0.7", {"start": v(108.98, 35.66) * mm, "mid": v(108.81, 35.4) * mm, "end": v(108.75, 35.1) * mm});
            skLineSegment(sketch, "E522.0.8", {"start": v(108.75, 35.1) * mm, "end": v(108.75, 31.5) * mm});
            skArc(sketch, "E522.0.9", {"start": v(108.75, 31.5) * mm, "mid": v(109.2, 30.45) * mm, "end": v(110.25, 30) * mm});
            skLineSegment(sketch, "E522.0.10", {"start": v(110.25, 30) * mm, "end": v(113.84, 30) * mm});
            skArc(sketch, "E522.0.11", {"start": v(113.84, 30) * mm, "mid": v(114.15, 30.07) * mm, "end": v(114.4, 30.24) * mm});
            skLineSegment(sketch, "E522.0.12", {"start": v(114.4, 30.24) * mm, "end": v(115.86, 31.7) * mm});
            skLineSegment(sketch, "E522.0.13", {"start": v(115.86, 31.7) * mm, "end": v(115.86, 31.8) * mm});
            skLineSegment(sketch, "E522.0.14", {"start": v(115.86, 31.8) * mm, "end": v(113.25, 31.8) * mm});
            skLineSegment(sketch, "E522.0.15", {"start": v(113.25, 31.8) * mm, "end": v(113.25, 33.45) * mm});
            skLineSegment(sketch, "E522.0.16", {"start": v(113.25, 33.45) * mm, "end": v(116.41, 36.6) * mm});
            skLineSegment(sketch, "E522.0.17", {"start": v(116.41, 36.6) * mm, "end": v(121.1, 36.6) * mm});
            skLineSegment(sketch, "E522.0.18", {"start": v(121.1, 36.6) * mm, "end": v(124.25, 33.45) * mm});
            skLineSegment(sketch, "E522.0.19", {"start": v(124.25, 33.45) * mm, "end": v(124.25, 31.8) * mm});
            skLineSegment(sketch, "E522.0.20", {"start": v(124.25, 31.8) * mm, "end": v(121.64, 31.8) * mm});
            skLineSegment(sketch, "E522.0.21", {"start": v(121.64, 31.8) * mm, "end": v(121.64, 31.7) * mm});
            skLineSegment(sketch, "E522.0.22", {"start": v(121.64, 31.7) * mm, "end": v(123.1, 30.24) * mm});
            skArc(sketch, "E522.0.23", {"start": v(123.1, 30.24) * mm, "mid": v(123.36, 30.07) * mm, "end": v(123.66, 30) * mm});
            skLineSegment(sketch, "E522.0.24", {"start": v(123.66, 30) * mm, "end": v(127.25, 30) * mm});
            skLineSegment(sketch, "E522.0.45", {"start": v(121.64, 48.32) * mm, "end": v(121.64, 48.2) * mm});
            skLineSegment(sketch, "E523.0", {"start": v(111.1, 33.44) * mm, "end": v(110.55, 33.44) * mm});
            skLineSegment(sketch, "E524.0", {"start": v(110.55, 33.44) * mm, "end": v(110.55, 31.8) * mm});
            skLineSegment(sketch, "E525.0", {"start": v(110.55, 31.8) * mm, "end": v(112.18, 31.8) * mm});
            skLineSegment(sketch, "E526.0", {"start": v(112.18, 31.8) * mm, "end": v(112.18, 32.35) * mm});
            skLineSegment(sketch, "E527.0", {"start": v(112.18, 32.35) * mm, "end": v(111.1, 33.44) * mm});
            skSolve(sketch);
        }
        {
            var Q0;
            Q0 = qSketchRegion(id + "F18", true);
            extrude(context, id + "F19", {"entities" : qUnion([Q0]), "depth" : 340 * mm, "offsetDistance" : 25 * mm});
        }
        {
            var Q0;
            Q0=qCreatedBy(makeId("Top.planeOp"),FACE);
            var sketch = newSketch(context, id + "F20", { "sketchPlane" : qUnion([Q0])});
            skLineSegment(sketch, "E528.bottom", {"start": v(624.15, 546.72) * mm, "end": v(924.15, 546.72) * mm});
            skLineSegment(sketch, "E528.top", {"start": v(624.15, 271.72) * mm, "end": v(924.15, 271.72) * mm});
            skLineSegment(sketch, "E528.left", {"start": v(624.15, 546.72) * mm, "end": v(624.15, 271.72) * mm});
            skLineSegment(sketch, "E528.right", {"start": v(924.15, 546.72) * mm, "end": v(924.15, 271.72) * mm});
            skLineSegment(sketch, "E529.bottom", {"start": v(904.15, 291.72) * mm, "end": v(644.15, 291.72) * mm});
            skLineSegment(sketch, "E529.top", {"start": v(904.15, 526.72) * mm, "end": v(644.15, 526.72) * mm});
            skLineSegment(sketch, "E529.left", {"start": v(904.15, 291.72) * mm, "end": v(904.15, 526.72) * mm});
            skLineSegment(sketch, "E529.right", {"start": v(644.15, 291.72) * mm, "end": v(644.15, 526.72) * mm});
            skPoint(sketch, "E529.middle", {"position": v(774.15, 409.22) * mm});
            skPoint(sketch, "E529.middle.positionSnap0", {"position": v(624.15, 409.22) * mm});
            skPoint(sketch, "E529.middle.positionSnap1", {"position": v(774.15, 546.72) * mm});
            skPoint(sketch, "E529.centerSnap0", {"position": v(624.15, 409.22) * mm});
            skPoint(sketch, "E529.centerSnap1", {"position": v(774.15, 546.72) * mm});
            skLineSegment(sketch, "E530", {"start": v(644.15, 526.72) * mm, "end": v(644.15, 546.72) * mm});
            skLineSegment(sketch, "E531", {"start": v(904.15, 526.72) * mm, "end": v(904.15, 546.72) * mm});
            skCircle(sketch, "E532", {"center": v(774.15, 282.39) * mm, "radius": 5.65 * mm});
            skPoint(sketch, "E532.centerSnap0", {"position": v(774.15, 291.72) * mm});
            skSolve(sketch);
        }
        {
            var Q0;
            Q0 = qSketchRegion(id + "F20", true);
            extrude(context, id + "F21", {"entities" : qUnion([Q0]), "depth" : 20 * mm, "offsetDistance" : 25 * mm});
        }
        {
            var Q0;
            Q0=qCreatedBy(makeId("Top.planeOp"),FACE);
            var sketch = newSketch(context, id + "F22", { "sketchPlane" : qUnion([Q0])});
            skLineSegment(sketch, "E533.bottom", {"start": v(1422.08, 301.13) * mm, "end": v(1462.08, 301.13) * mm});
            skLineSegment(sketch, "E533.top", {"start": v(1422.08, 286.13) * mm, "end": v(1462.08, 286.13) * mm});
            skLineSegment(sketch, "E533.left", {"start": v(1422.08, 301.13) * mm, "end": v(1422.08, 286.13) * mm});
            skLineSegment(sketch, "E533.right", {"start": v(1462.08, 301.13) * mm, "end": v(1462.08, 286.13) * mm});
            skCircle(sketch, "E534", {"center": v(1442.08, 294.13) * mm, "radius": 2 * mm});
            skPoint(sketch, "E534.centerSnap0", {"position": v(1442.08, 301.13) * mm});
            skLineSegment(sketch, "E535", {"start": v(1442.08, 294.13) * mm, "end": v(1442.08, 286.13) * mm, "construction": true});
            skSolve(sketch);
        }
        {
            var Q0;
            Q0 = qSketchRegion(id + "F22", true);
            extrude(context, id + "F23", {"entities" : qUnion([Q0]), "depth" : 20 * mm, "offsetDistance" : 25 * mm});
        }
        {
            var Q0;
            Q0=makeQuery(id+"F23.opExtrude","SWEPT_FACE",FACE,{"disambiguationData":[OSD([sQuery(id+"F22.wireOp",EDGE,"E533.bottom")])]});
            var sketch = newSketch(context, id + "F24", { "sketchPlane" : qUnion([Q0])});
            skLineSegment(sketch, "E536", {"start": v(-1442.08, 20) * mm, "end": v(-1442.08, 0) * mm, "construction": true});
            skLineSegment(sketch, "E537", {"start": v(-1462.08, 10) * mm, "end": v(-1422.08, 10) * mm, "construction": true});
            skCircle(sketch, "E538", {"center": v(-1455.17, 10) * mm, "radius": 6 * mm});
            skCircle(sketch, "E539.MirrorC", {"center": v(-1429, 10) * mm, "radius": 6 * mm});
            skSolve(sketch);
        }
        {
            var Q0;
            Q0 = qSketchRegion(id + "F24", true);
            extrude(context, id + "F25", {"entities" : qUnion([Q0]), "operationType" : NewBodyOperationType.REMOVE, "oppositeDirection" : true, "depth" : 10 * mm, "offsetDistance" : 25 * mm});
        }
        {
            var Q0;
            Q0=makeQuery(id+"F23.opExtrude","SWEPT_FACE",FACE,{"disambiguationData":[OSD([sQuery(id+"F22.wireOp",EDGE,"E533.bottom")])]});
            var sketch = newSketch(context, id + "F26", { "sketchPlane" : qUnion([Q0])});
            skCircle(sketch, "E540", {"center": v(-1455.17, 10) * mm, "radius": 2.75 * mm});
            skCircle(sketch, "E541", {"center": v(-1429, 10) * mm, "radius": 2.75 * mm});
            skSolve(sketch);
        }
        {
            var Q0;
            Q0 = qSketchRegion(id + "F26", true);
            extrude(context, id + "F27", {"entities" : qUnion([Q0]), "operationType" : NewBodyOperationType.REMOVE, "oppositeDirection" : true, "depth" : 25 * mm, "offsetDistance" : 25 * mm});
        }
        {
            var Q0;
            Q0=makeQuery(id+"F23.opExtrude","SWEPT_EDGE",EDGE,{"disambiguationData":[OSD([sQuery(id+"F22.wireOp",EDGE,"E533.bottom"),sQuery(id+"F22.wireOp",EDGE,"E533.left")])]});
            var Q1;
            Q1=makeQuery(id+"F23.opExtrude","SWEPT_EDGE",EDGE,{"disambiguationData":[OSD([sQuery(id+"F22.wireOp",EDGE,"E533.bottom"),sQuery(id+"F22.wireOp",EDGE,"E533.right")])]});
            chamfer(context, id + "F28", {"entities" : qUnion([Q0, Q1]), "width" : 13 * mm, "tangentPropagation" : true});
        }
        {
            var Q0;
            Q0=qCreatedBy(makeId("Top.planeOp"),FACE);
            var sketch = newSketch(context, id + "F29", { "sketchPlane" : qUnion([Q0])});
            skLineSegment(sketch, "E542.bottom", {"start": v(1514.38, 286.76) * mm, "end": v(1554.38, 286.76) * mm});
            skLineSegment(sketch, "E542.left", {"start": v(1514.38, 286.76) * mm, "end": v(1514.38, 310.4) * mm});
            skLineSegment(sketch, "E542.right", {"start": v(1554.38, 286.76) * mm, "end": v(1554.38, 310.4) * mm});
            skCircle(sketch, "E543", {"center": v(1534.38, 304.26) * mm, "radius": 2 * mm});
            skPoint(sketch, "E543.centerSnap0", {"position": v(1534.38, 316.76) * mm});
            skLineSegment(sketch, "E544", {"start": v(1514.38, 310.4) * mm, "end": v(1554.38, 310.4) * mm});
            skLineSegment(sketch, "E545", {"start": v(1534.38, 304.26) * mm, "end": v(1534.38, 286.76) * mm, "construction": true});
            skPoint(sketch, "E546.orphan", {"position": v(1514.38, 316.76) * mm});
            skPoint(sketch, "E547.orphan", {"position": v(1554.38, 316.76) * mm});
            skSolve(sketch);
        }
        {
            var Q0;
            Q0 = qSketchRegion(id + "F29", true);
            extrude(context, id + "F30", {"entities" : qUnion([Q0]), "depth" : 20 * mm, "offsetDistance" : 25 * mm});
        }
        {
            var Q0;
            Q0=makeQuery(id+"F30.opExtrude","SWEPT_FACE",FACE,{"disambiguationData":[OSD([sQuery(id+"F29.wireOp",EDGE,"E544")])]});
            var sketch = newSketch(context, id + "F31", { "sketchPlane" : qUnion([Q0])});
            skLineSegment(sketch, "E548", {"start": v(-1534.38, 20) * mm, "end": v(-1534.38, 0) * mm, "construction": true});
            skLineSegment(sketch, "E549", {"start": v(-1554.38, 10) * mm, "end": v(-1514.38, 10) * mm, "construction": true});
            skCircle(sketch, "E550", {"center": v(-1547.58, 10) * mm, "radius": 6 * mm});
            skCircle(sketch, "E551.MirrorC", {"center": v(-1521.18, 10) * mm, "radius": 6 * mm});
            skSolve(sketch);
        }
        {
            var Q0;
            Q0 = qSketchRegion(id + "F31", true);
            extrude(context, id + "F32", {"entities" : qUnion([Q0]), "operationType" : NewBodyOperationType.REMOVE, "oppositeDirection" : true, "depth" : 18 * mm, "offsetDistance" : 25 * mm});
        }
        {
            var Q0;
            Q0=makeQuery(id+"F30.opExtrude","SWEPT_FACE",FACE,{"disambiguationData":[OSD([sQuery(id+"F29.wireOp",EDGE,"E544")])]});
            var sketch = newSketch(context, id + "F33", { "sketchPlane" : qUnion([Q0])});
            skCircle(sketch, "E552", {"center": v(-1547.58, 10) * mm, "radius": 2.25 * mm});
            skCircle(sketch, "E553", {"center": v(-1521.18, 10) * mm, "radius": 2.25 * mm});
            skSolve(sketch);
        }
        {
            var Q0;
            Q0 = qSketchRegion(id + "F33", true);
            extrude(context, id + "F34", {"entities" : qUnion([Q0]), "operationType" : NewBodyOperationType.REMOVE, "oppositeDirection" : true, "depth" : 25 * mm, "offsetDistance" : 25 * mm});
        }
        {
            var Q0;
            Q0=makeQuery(id+"F30.opExtrude","SWEPT_EDGE",EDGE,{"disambiguationData":[OSD([sQuery(id+"F29.wireOp",EDGE,"E542.right"),sQuery(id+"F29.wireOp",EDGE,"E544")])]});
            var Q1;
            Q1=makeQuery(id+"F30.opExtrude","SWEPT_EDGE",EDGE,{"disambiguationData":[OSD([sQuery(id+"F29.wireOp",EDGE,"E542.left"),sQuery(id+"F29.wireOp",EDGE,"E544")])]});
            chamfer(context, id + "F35", {"entities" : qUnion([Q0, Q1]), "width" : 12 * mm, "tangentPropagation" : true});
        }
        {
            var Q0;
            Q0=makeQuery(id+"F30.opExtrude","SWEPT_FACE",FACE,{"disambiguationData":[OSD([sQuery(id+"F29.wireOp",EDGE,"E544")])]});
            var sketch = newSketch(context, id + "F36", { "sketchPlane" : qUnion([Q0])});
            skLineSegment(sketch, "E554.bottom", {"start": v(-1526.38, 0) * mm, "end": v(-1541.92, 0) * mm, "construction": true});
            skLineSegment(sketch, "E554.top", {"start": v(-1526.38, 8) * mm, "end": v(-1541.92, 8) * mm, "construction": true});
            skLineSegment(sketch, "E554.left", {"start": v(-1526.38, 0) * mm, "end": v(-1526.38, 8) * mm, "construction": true});
            skLineSegment(sketch, "E554.right", {"start": v(-1541.92, 0) * mm, "end": v(-1541.92, 8) * mm, "construction": true});
            skLineSegment(sketch, "E555.bottom", {"start": v(-1511.72, 8) * mm, "end": v(-1558.95, 8) * mm});
            skLineSegment(sketch, "E555.top", {"start": v(-1511.72, 25.09) * mm, "end": v(-1558.95, 25.09) * mm});
            skLineSegment(sketch, "E555.left", {"start": v(-1511.72, 8) * mm, "end": v(-1511.72, 25.09) * mm});
            skLineSegment(sketch, "E555.right", {"start": v(-1558.95, 8) * mm, "end": v(-1558.95, 25.09) * mm});
            skSolve(sketch);
        }
        {
            var Q0;
            Q0 = qSketchRegion(id + "F36", true);
            extrude(context, id + "F37", {"entities" : qUnion([Q0]), "operationType" : NewBodyOperationType.REMOVE, "oppositeDirection" : true, "depth" : 18 * mm, "offsetDistance" : 25 * mm});
        }
        {
            var Q0;
            {var subQ0=sQuery(id+"F31.wireOp",EDGE,"E551.MirrorC");var subQ1=sQuery(id+"F31.wireOp",EDGE,"E550");var subQ2=sQuery(id+"F36.wireOp",EDGE,"E555.bottom");Q0=makeQuery(id+"F37.boolean.opBoolean","COPY",EDGE,{"disambiguationData":[TD([makeQuery(id+"F32.boolean.opBoolean","COPY",FACE,{"derivedFrom":makeQuery(id+"F32.opExtrude","SWEPT_FACE",FACE,{"disambiguationData":[OSD([subQ1])]})}),makeQuery(id+"F32.boolean.opBoolean","COPY",FACE,{"derivedFrom":makeQuery(id+"F32.opExtrude","CAP_FACE",FACE,{"disambiguationData":[OSD([subQ1])],"isStart":false})}),makeQuery(id+"F32.boolean.opBoolean","COPY",FACE,{"derivedFrom":makeQuery(id+"F32.opExtrude","SWEPT_FACE",FACE,{"disambiguationData":[OSD([subQ0])]})}),makeQuery(id+"F32.boolean.opBoolean","COPY",FACE,{"derivedFrom":makeQuery(id+"F32.opExtrude","CAP_FACE",FACE,{"disambiguationData":[OSD([subQ0])],"isStart":false})}),makeQuery(id+"F37.opExtrude","SWEPT_FACE",FACE,{"disambiguationData":[OSD([subQ2])]}),makeQuery(id+"F37.opExtrude","CAP_FACE",FACE,{"disambiguationData":[OSD([subQ2,sQuery(id+"F36.wireOp",EDGE,"E555.top"),sQuery(id+"F36.wireOp",EDGE,"E555.left"),sQuery(id+"F36.wireOp",EDGE,"E555.right")])],"isStart":false})])],"derivedFrom":makeQuery(id+"F37.opExtrude","CAP_EDGE",EDGE,{"disambiguationData":[OSD([subQ2])],"isStart":false})});}
            var Q1;
            Q1=makeQuery(id+"F30.opExtrude","CAP_EDGE",EDGE,{"disambiguationData":[OSD([sQuery(id+"F29.wireOp",EDGE,"E542.right")])],"isStart":false});
            var Q2;
            Q2=makeQuery(id+"F30.opExtrude","CAP_EDGE",EDGE,{"disambiguationData":[OSD([sQuery(id+"F29.wireOp",EDGE,"E542.left")])],"isStart":false});
            var Q3;
            {var subQ0=sQuery(id+"F31.wireOp",EDGE,"E550");var subQ1=sQuery(id+"F36.wireOp",EDGE,"E555.bottom");Q3=makeQuery(id+"F37.boolean.opBoolean","COPY",EDGE,{"disambiguationData":[TD([makeQuery(id+"F30.opExtrude","SWEPT_FACE",FACE,{"disambiguationData":[OSD([sQuery(id+"F29.wireOp",EDGE,"E542.right")])]}),makeQuery(id+"F32.boolean.opBoolean","COPY",FACE,{"derivedFrom":makeQuery(id+"F32.opExtrude","SWEPT_FACE",FACE,{"disambiguationData":[OSD([subQ0])]})}),makeQuery(id+"F32.boolean.opBoolean","COPY",FACE,{"derivedFrom":makeQuery(id+"F32.opExtrude","CAP_FACE",FACE,{"disambiguationData":[OSD([subQ0])],"isStart":false})}),makeQuery(id+"F32.boolean.opBoolean","COPY",FACE,{"derivedFrom":makeQuery(id+"F32.opExtrude","CAP_FACE",FACE,{"disambiguationData":[OSD([sQuery(id+"F31.wireOp",EDGE,"E551.MirrorC")])],"isStart":false})}),makeQuery(id+"F37.opExtrude","SWEPT_FACE",FACE,{"disambiguationData":[OSD([subQ1])]}),makeQuery(id+"F37.opExtrude","CAP_FACE",FACE,{"disambiguationData":[OSD([subQ1,sQuery(id+"F36.wireOp",EDGE,"E555.top"),sQuery(id+"F36.wireOp",EDGE,"E555.left"),sQuery(id+"F36.wireOp",EDGE,"E555.right")])],"isStart":false})])],"derivedFrom":makeQuery(id+"F37.opExtrude","CAP_EDGE",EDGE,{"disambiguationData":[OSD([subQ1])],"isStart":false})});}
            var Q4;
            {var subQ0=sQuery(id+"F31.wireOp",EDGE,"E551.MirrorC");var subQ1=sQuery(id+"F36.wireOp",EDGE,"E555.bottom");Q4=makeQuery(id+"F37.boolean.opBoolean","COPY",EDGE,{"disambiguationData":[TD([makeQuery(id+"F30.opExtrude","SWEPT_FACE",FACE,{"disambiguationData":[OSD([sQuery(id+"F29.wireOp",EDGE,"E542.left")])]}),makeQuery(id+"F32.boolean.opBoolean","COPY",FACE,{"derivedFrom":makeQuery(id+"F32.opExtrude","CAP_FACE",FACE,{"disambiguationData":[OSD([sQuery(id+"F31.wireOp",EDGE,"E550")])],"isStart":false})}),makeQuery(id+"F32.boolean.opBoolean","COPY",FACE,{"derivedFrom":makeQuery(id+"F32.opExtrude","SWEPT_FACE",FACE,{"disambiguationData":[OSD([subQ0])]})}),makeQuery(id+"F32.boolean.opBoolean","COPY",FACE,{"derivedFrom":makeQuery(id+"F32.opExtrude","CAP_FACE",FACE,{"disambiguationData":[OSD([subQ0])],"isStart":false})}),makeQuery(id+"F37.opExtrude","SWEPT_FACE",FACE,{"disambiguationData":[OSD([subQ1])]}),makeQuery(id+"F37.opExtrude","CAP_FACE",FACE,{"disambiguationData":[OSD([subQ1,sQuery(id+"F36.wireOp",EDGE,"E555.top"),sQuery(id+"F36.wireOp",EDGE,"E555.left"),sQuery(id+"F36.wireOp",EDGE,"E555.right")])],"isStart":false})])],"derivedFrom":makeQuery(id+"F37.opExtrude","CAP_EDGE",EDGE,{"disambiguationData":[OSD([subQ1])],"isStart":false})});}
            var Q5;
            Q5=makeQuery(id+"F30.opExtrude","CAP_EDGE",EDGE,{"disambiguationData":[OSD([sQuery(id+"F29.wireOp",EDGE,"E542.left")])],"isStart":true});
            var Q6;
            Q6=makeQuery(id+"F30.opExtrude","CAP_EDGE",EDGE,{"disambiguationData":[OSD([sQuery(id+"F29.wireOp",EDGE,"E542.right")])],"isStart":true});
            chamfer(context, id + "F38", {"entities" : qUnion([Q0, Q1, Q2, Q3, Q4, Q5, Q6]), "width" : 5 * mm, "tangentPropagation" : true});
        }
        {
            var Q0;
            Q0=makeQuery(id+"F23.opExtrude","SWEPT_FACE",FACE,{"disambiguationData":[OSD([sQuery(id+"F22.wireOp",EDGE,"E533.bottom")])]});
            var sketch = newSketch(context, id + "F39", { "sketchPlane" : qUnion([Q0])});
            skLineSegment(sketch, "E556.bottom", {"start": v(-1435.08, 0) * mm, "end": v(-1449.08, 0) * mm, "construction": true});
            skLineSegment(sketch, "E556.top", {"start": v(-1435.08, 8) * mm, "end": v(-1449.08, 8) * mm, "construction": true});
            skLineSegment(sketch, "E556.left", {"start": v(-1435.08, 0) * mm, "end": v(-1435.08, 8) * mm, "construction": true});
            skLineSegment(sketch, "E556.right", {"start": v(-1449.08, 0) * mm, "end": v(-1449.08, 8) * mm, "construction": true});
            skLineSegment(sketch, "E557.bottom", {"start": v(-1414.47, 8) * mm, "end": v(-1467.45, 8) * mm});
            skLineSegment(sketch, "E557.top", {"start": v(-1414.47, 25.04) * mm, "end": v(-1467.45, 25.04) * mm});
            skLineSegment(sketch, "E557.left", {"start": v(-1414.47, 8) * mm, "end": v(-1414.47, 25.04) * mm});
            skLineSegment(sketch, "E557.right", {"start": v(-1467.45, 8) * mm, "end": v(-1467.45, 25.04) * mm});
            skSolve(sketch);
        }
        {
            var Q0;
            Q0 = qSketchRegion(id + "F39", true);
            extrude(context, id + "F40", {"entities" : qUnion([Q0]), "operationType" : NewBodyOperationType.REMOVE, "oppositeDirection" : true, "depth" : 10 * mm, "offsetDistance" : 25 * mm});
        }
        {
            var Q0;
            Q0=makeQuery(id+"F23.opExtrude","CAP_FACE",FACE,{"disambiguationData":[OSD([sQuery(id+"F22.wireOp",EDGE,"E533.bottom"),sQuery(id+"F22.wireOp",EDGE,"E533.top"),sQuery(id+"F22.wireOp",EDGE,"E533.left"),sQuery(id+"F22.wireOp",EDGE,"E533.right"),sQuery(id+"F22.wireOp",EDGE,"E534")])],"isStart":false});
            var sketch = newSketch(context, id + "F41", { "sketchPlane" : qUnion([Q0])});
            skCircle(sketch, "E558", {"center": v(1442.1, 294.4) * mm, "radius": 7.61 * mm});
            skSolve(sketch);
        }
        {
            var Q0;
            Q0 = qSketchRegion(id + "F41", true);
            extrude(context, id + "F42", {"entities" : qUnion([Q0]), "operationType" : NewBodyOperationType.REMOVE, "oppositeDirection" : true, "depth" : 12 * mm, "offsetDistance" : 25 * mm});
        }
        {
            var Q0;
            Q0=makeQuery(id+"F23.opExtrude","CAP_EDGE",EDGE,{"disambiguationData":[OSD([sQuery(id+"F22.wireOp",EDGE,"E533.right")])],"isStart":true});
            var Q1;
            Q1=makeQuery(id+"F23.opExtrude","CAP_EDGE",EDGE,{"disambiguationData":[OSD([sQuery(id+"F22.wireOp",EDGE,"E533.left")])],"isStart":true});
            var Q2;
            Q2=makeQuery(id+"F23.opExtrude","CAP_EDGE",EDGE,{"disambiguationData":[OSD([sQuery(id+"F22.wireOp",EDGE,"E533.left")])],"isStart":false});
            var Q3;
            Q3=makeQuery(id+"F23.opExtrude","CAP_EDGE",EDGE,{"disambiguationData":[OSD([sQuery(id+"F22.wireOp",EDGE,"E533.right")])],"isStart":false});
            chamfer(context, id + "F43", {"entities" : qUnion([Q0, Q1, Q2, Q3]), "width" : 5 * mm, "tangentPropagation" : true});
        }
        {
            var Q0;
            Q0=makeQuery(id+"F42.boolean.opBoolean","COPY",EDGE,{"derivedFrom":makeQuery(id+"F42.opExtrude","CAP_EDGE",EDGE,{"disambiguationData":[OSD([sQuery(id+"F41.wireOp",EDGE,"E558")])],"isStart":false})});
            chamfer(context, id + "F44", {"entities" : qUnion([Q0]), "width" : 2 * mm, "tangentPropagation" : true});
        }
    });
